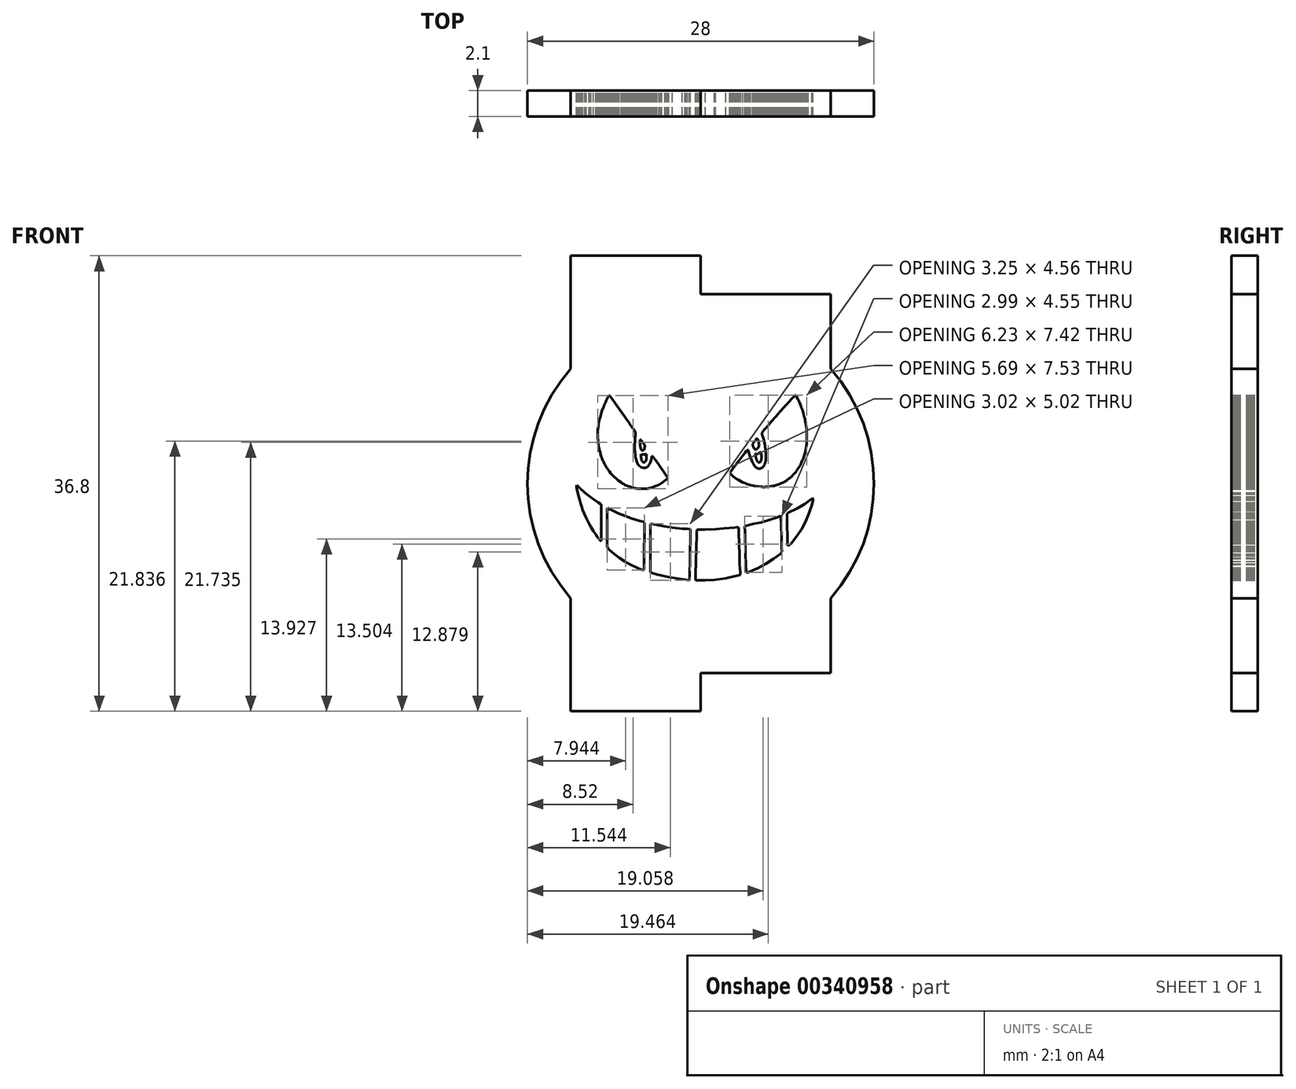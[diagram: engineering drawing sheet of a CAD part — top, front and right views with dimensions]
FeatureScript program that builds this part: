
annotation { "Feature Type Name" : "Feature", "Feature Type Description" : "" }
export const myFeature = defineFeature(function(context is Context, id is Id, definition is map)
    precondition{}
    {
        {
            var Q0;
            Q0=qCreatedBy(makeId("Front.planeOp"),FACE);
            var sketch = newSketch(context, id + "F0", { "sketchPlane" : qUnion([Q0])});
            skArc(sketch, "E0", {"start": v(-10.5, 9.26) * mm, "mid": v(-14, 0) * mm, "end": v(-10.5, -9.26) * mm});
            skLineSegment(sketch, "E1", {"start": v(-10.5, 9.26) * mm, "end": v(-10.5, 18.4) * mm});
            skLineSegment(sketch, "E2", {"start": v(-10.5, 18.4) * mm, "end": v(0, 18.4) * mm});
            skLineSegment(sketch, "E3", {"start": v(0, 18.4) * mm, "end": v(0, 15.3) * mm});
            skLineSegment(sketch, "E4", {"start": v(0, 15.3) * mm, "end": v(10.5, 15.3) * mm});
            skLineSegment(sketch, "E5", {"start": v(10.5, 15.3) * mm, "end": v(10.5, 9.26) * mm});
            skLineSegment(sketch, "E6", {"start": v(-10.5, -9.26) * mm, "end": v(-10.5, -18.4) * mm});
            skLineSegment(sketch, "E7", {"start": v(-10.5, -18.4) * mm, "end": v(0, -18.4) * mm});
            skLineSegment(sketch, "E8", {"start": v(0, -18.4) * mm, "end": v(0, -15.3) * mm});
            skLineSegment(sketch, "E9", {"start": v(0, -15.3) * mm, "end": v(10.5, -15.3) * mm});
            skLineSegment(sketch, "E10", {"start": v(10.5, -15.3) * mm, "end": v(10.5, -9.26) * mm});
            skArc(sketch, "E11.trimOffspring", {"start": v(10.5, -9.26) * mm, "mid": v(14, 0) * mm, "end": v(10.5, 9.26) * mm});
            skSolve(sketch);
        }
        {
            var Q0;
            Q0 = qSketchRegion(id + "F0", true);
            var Q1;
            Q1=makeQuery(id+"F0.imprint","IMPRINT",FACE,{"disambiguationData":[TD([[makeQuery(id+"F0.imprint","IMPRINT",EDGE,{"derivedFrom":sQuery(id+"F0.wireOp",EDGE,"E0")}),1.0]])]});
            extrude(context, id + "F1", {"entities" : qUnion([Q0, Q1]), "depth" : 2.1 * mm});
        }
        {
            var Q0;
            Q0=qCreatedBy(makeId("Front.planeOp"),FACE);
            var sketch = newSketch(context, id + "F2", { "sketchPlane" : qUnion([Q0])});
            skLineSegment(sketch, "E12", {"start": v(-7.31, 7.04) * mm, "end": v(-7.08, 6.7) * mm});
            skLineSegment(sketch, "E13", {"start": v(-7.08, 6.7) * mm, "end": v(-6.95, 6.53) * mm});
            skLineSegment(sketch, "E14", {"start": v(-6.95, 6.53) * mm, "end": v(-6.8, 6.32) * mm});
            skLineSegment(sketch, "E15", {"start": v(-6.8, 6.32) * mm, "end": v(-6.71, 6.2) * mm});
            skLineSegment(sketch, "E16", {"start": v(-6.71, 6.2) * mm, "end": v(-6.65, 6.1) * mm});
            skLineSegment(sketch, "E17", {"start": v(-6.65, 6.1) * mm, "end": v(-6.58, 6) * mm});
            skLineSegment(sketch, "E18", {"start": v(-6.58, 6) * mm, "end": v(-6.47, 5.86) * mm});
            skLineSegment(sketch, "E19", {"start": v(-6.47, 5.86) * mm, "end": v(-6.39, 5.75) * mm});
            skLineSegment(sketch, "E20", {"start": v(-6.39, 5.75) * mm, "end": v(-6.31, 5.64) * mm});
            skLineSegment(sketch, "E21", {"start": v(-6.31, 5.64) * mm, "end": v(-6.24, 5.54) * mm});
            skLineSegment(sketch, "E22", {"start": v(-6.24, 5.54) * mm, "end": v(-6.17, 5.44) * mm});
            skLineSegment(sketch, "E23", {"start": v(-6.17, 5.44) * mm, "end": v(-6.07, 5.3) * mm});
            skLineSegment(sketch, "E24", {"start": v(-6.07, 5.3) * mm, "end": v(-5.98, 5.18) * mm});
            skLineSegment(sketch, "E25", {"start": v(-5.98, 5.18) * mm, "end": v(-5.91, 5.08) * mm});
            skLineSegment(sketch, "E26", {"start": v(-5.91, 5.08) * mm, "end": v(-5.84, 4.97) * mm});
            skLineSegment(sketch, "E27", {"start": v(-5.84, 4.97) * mm, "end": v(-5.76, 4.87) * mm});
            skLineSegment(sketch, "E28", {"start": v(-5.76, 4.87) * mm, "end": v(-5.68, 4.74) * mm});
            skLineSegment(sketch, "E29", {"start": v(-5.68, 4.74) * mm, "end": v(-5.6, 4.64) * mm});
            skLineSegment(sketch, "E30", {"start": v(-5.6, 4.64) * mm, "end": v(-5.54, 4.54) * mm});
            skLineSegment(sketch, "E31", {"start": v(-5.54, 4.54) * mm, "end": v(-5.47, 4.44) * mm});
            skLineSegment(sketch, "E32", {"start": v(-5.47, 4.44) * mm, "end": v(-5.42, 4.38) * mm});
            skLineSegment(sketch, "E33", {"start": v(-5.42, 4.38) * mm, "end": v(-5.35, 4.28) * mm});
            skLineSegment(sketch, "E34", {"start": v(-5.35, 4.28) * mm, "end": v(-5.31, 4.23) * mm});
            skLineSegment(sketch, "E35", {"start": v(-5.31, 4.23) * mm, "end": v(-5.3, 4.2) * mm});
            skLineSegment(sketch, "E36", {"start": v(-5.3, 4.2) * mm, "end": v(-5.28, 4.18) * mm});
            skLineSegment(sketch, "E37", {"start": v(-5.28, 4.18) * mm, "end": v(-5.27, 4.16) * mm});
            skLineSegment(sketch, "E38", {"start": v(-5.27, 4.16) * mm, "end": v(-5.27, 4.12) * mm});
            skLineSegment(sketch, "E39", {"start": v(-5.27, 4.12) * mm, "end": v(-5.27, 4.06) * mm});
            skLineSegment(sketch, "E40", {"start": v(-5.27, 4.06) * mm, "end": v(-5.27, 4) * mm});
            skLineSegment(sketch, "E41", {"start": v(-5.27, 4) * mm, "end": v(-5.29, 3.9) * mm});
            skLineSegment(sketch, "E42", {"start": v(-5.29, 3.9) * mm, "end": v(-5.3, 3.83) * mm});
            skLineSegment(sketch, "E43", {"start": v(-5.3, 3.83) * mm, "end": v(-5.3, 3.75) * mm});
            skLineSegment(sketch, "E44", {"start": v(-5.3, 3.75) * mm, "end": v(-5.31, 3.65) * mm});
            skLineSegment(sketch, "E45", {"start": v(-5.31, 3.65) * mm, "end": v(-5.31, 3.58) * mm});
            skLineSegment(sketch, "E46", {"start": v(-5.31, 3.58) * mm, "end": v(-5.32, 3.51) * mm});
            skLineSegment(sketch, "E47", {"start": v(-5.32, 3.51) * mm, "end": v(-5.32, 3.46) * mm});
            skLineSegment(sketch, "E48", {"start": v(-5.32, 3.46) * mm, "end": v(-5.32, 3.4) * mm});
            skLineSegment(sketch, "E49", {"start": v(-5.32, 3.4) * mm, "end": v(-5.32, 3.32) * mm});
            skLineSegment(sketch, "E50", {"start": v(-5.32, 3.32) * mm, "end": v(-5.33, 3.26) * mm});
            skLineSegment(sketch, "E51", {"start": v(-5.33, 3.26) * mm, "end": v(-5.34, 3.2) * mm});
            skLineSegment(sketch, "E52", {"start": v(-5.34, 3.2) * mm, "end": v(-5.34, 3.13) * mm});
            skLineSegment(sketch, "E53", {"start": v(-5.34, 3.13) * mm, "end": v(-5.34, 3.06) * mm});
            skLineSegment(sketch, "E54", {"start": v(-5.34, 3.06) * mm, "end": v(-5.34, 3) * mm});
            skLineSegment(sketch, "E55", {"start": v(-5.34, 3) * mm, "end": v(-5.34, 2.93) * mm});
            skLineSegment(sketch, "E56", {"start": v(-5.34, 2.93) * mm, "end": v(-5.34, 2.87) * mm});
            skPoint(sketch, "E56.endSnap0", {"position": v(-5.34, 2.96) * mm});
            skLineSegment(sketch, "E57", {"start": v(-5.34, 2.87) * mm, "end": v(-5.34, 2.8) * mm});
            skLineSegment(sketch, "E58", {"start": v(-5.34, 2.8) * mm, "end": v(-5.33, 2.7) * mm});
            skLineSegment(sketch, "E59", {"start": v(-5.33, 2.7) * mm, "end": v(-5.32, 2.62) * mm});
            skLineSegment(sketch, "E60", {"start": v(-5.32, 2.62) * mm, "end": v(-5.32, 2.53) * mm});
            skLineSegment(sketch, "E61", {"start": v(-5.32, 2.53) * mm, "end": v(-5.3, 2.43) * mm});
            skLineSegment(sketch, "E62", {"start": v(-5.3, 2.43) * mm, "end": v(-5.29, 2.34) * mm});
            skLineSegment(sketch, "E63", {"start": v(-5.29, 2.34) * mm, "end": v(-5.29, 2.26) * mm});
            skLineSegment(sketch, "E64", {"start": v(-5.29, 2.26) * mm, "end": v(-5.27, 2.16) * mm});
            skLineSegment(sketch, "E65", {"start": v(-5.27, 2.16) * mm, "end": v(-5.25, 2.04) * mm});
            skLineSegment(sketch, "E66", {"start": v(-5.25, 2.04) * mm, "end": v(-5.22, 1.94) * mm});
            skLineSegment(sketch, "E67", {"start": v(-5.22, 1.94) * mm, "end": v(-5.18, 1.82) * mm});
            skLineSegment(sketch, "E68", {"start": v(-5.18, 1.82) * mm, "end": v(-5.14, 1.72) * mm});
            skLineSegment(sketch, "E69", {"start": v(-5.14, 1.72) * mm, "end": v(-5.11, 1.64) * mm});
            skLineSegment(sketch, "E70", {"start": v(-5.11, 1.64) * mm, "end": v(-5.07, 1.57) * mm});
            skLineSegment(sketch, "E71", {"start": v(-5.07, 1.57) * mm, "end": v(-5.04, 1.5) * mm});
            skLineSegment(sketch, "E72", {"start": v(-5.04, 1.5) * mm, "end": v(-5, 1.46) * mm});
            skLineSegment(sketch, "E73", {"start": v(-5, 1.46) * mm, "end": v(-4.96, 1.42) * mm});
            skLineSegment(sketch, "E74", {"start": v(-4.96, 1.42) * mm, "end": v(-4.91, 1.38) * mm});
            skLineSegment(sketch, "E75", {"start": v(-4.91, 1.38) * mm, "end": v(-4.88, 1.35) * mm});
            skLineSegment(sketch, "E76", {"start": v(-4.88, 1.35) * mm, "end": v(-4.83, 1.32) * mm});
            skLineSegment(sketch, "E77", {"start": v(-4.83, 1.32) * mm, "end": v(-4.8, 1.3) * mm});
            skLineSegment(sketch, "E78", {"start": v(-4.8, 1.3) * mm, "end": v(-4.75, 1.28) * mm});
            skLineSegment(sketch, "E79", {"start": v(-4.75, 1.28) * mm, "end": v(-4.72, 1.28) * mm});
            skLineSegment(sketch, "E80", {"start": v(-4.72, 1.28) * mm, "end": v(-4.67, 1.27) * mm});
            skLineSegment(sketch, "E81", {"start": v(-4.67, 1.27) * mm, "end": v(-4.62, 1.27) * mm});
            skLineSegment(sketch, "E82", {"start": v(-4.62, 1.27) * mm, "end": v(-4.57, 1.27) * mm});
            skLineSegment(sketch, "E83", {"start": v(-4.57, 1.27) * mm, "end": v(-4.52, 1.27) * mm});
            skLineSegment(sketch, "E84", {"start": v(-4.52, 1.27) * mm, "end": v(-4.48, 1.27) * mm});
            skLineSegment(sketch, "E85", {"start": v(-4.48, 1.27) * mm, "end": v(-4.42, 1.3) * mm});
            skLineSegment(sketch, "E86", {"start": v(-4.42, 1.3) * mm, "end": v(-4.37, 1.31) * mm});
            skLineSegment(sketch, "E87", {"start": v(-4.37, 1.31) * mm, "end": v(-4.33, 1.34) * mm});
            skLineSegment(sketch, "E88", {"start": v(-4.33, 1.34) * mm, "end": v(-4.3, 1.37) * mm});
            skLineSegment(sketch, "E89", {"start": v(-4.3, 1.37) * mm, "end": v(-4.26, 1.4) * mm});
            skLineSegment(sketch, "E90", {"start": v(-4.26, 1.4) * mm, "end": v(-4.22, 1.44) * mm});
            skLineSegment(sketch, "E91", {"start": v(-4.22, 1.44) * mm, "end": v(-4.18, 1.48) * mm});
            skLineSegment(sketch, "E92", {"start": v(-4.18, 1.48) * mm, "end": v(-4.15, 1.53) * mm});
            skLineSegment(sketch, "E93", {"start": v(-4.15, 1.53) * mm, "end": v(-4.12, 1.58) * mm});
            skLineSegment(sketch, "E94", {"start": v(-4.12, 1.58) * mm, "end": v(-4.1, 1.64) * mm});
            skLineSegment(sketch, "E95", {"start": v(-4.1, 1.64) * mm, "end": v(-4.08, 1.7) * mm});
            skLineSegment(sketch, "E96", {"start": v(-4.08, 1.7) * mm, "end": v(-4.05, 1.78) * mm});
            skLineSegment(sketch, "E97", {"start": v(-4.05, 1.78) * mm, "end": v(-4.02, 1.87) * mm});
            skLineSegment(sketch, "E98", {"start": v(-4.02, 1.87) * mm, "end": v(-4, 1.94) * mm});
            skLineSegment(sketch, "E99", {"start": v(-4, 1.94) * mm, "end": v(-3.99, 2) * mm});
            skLineSegment(sketch, "E100", {"start": v(-3.99, 2) * mm, "end": v(-3.98, 2.05) * mm});
            skLineSegment(sketch, "E101", {"start": v(-3.98, 2.05) * mm, "end": v(-3.96, 2.1) * mm});
            skLineSegment(sketch, "E102", {"start": v(-3.96, 2.1) * mm, "end": v(-3.94, 2.18) * mm});
            skLineSegment(sketch, "E103", {"start": v(-3.94, 2.18) * mm, "end": v(-3.93, 2.22) * mm});
            skLineSegment(sketch, "E104", {"start": v(-3.93, 2.22) * mm, "end": v(-3.93, 2.23) * mm});
            skLineSegment(sketch, "E105", {"start": v(-3.93, 2.23) * mm, "end": v(-3.92, 2.23) * mm});
            skLineSegment(sketch, "E106", {"start": v(-3.92, 2.23) * mm, "end": v(-3.9, 2.22) * mm});
            skLineSegment(sketch, "E107", {"start": v(-3.9, 2.22) * mm, "end": v(-3.86, 2.16) * mm});
            skLineSegment(sketch, "E108", {"start": v(-3.86, 2.16) * mm, "end": v(-3.8, 2.1) * mm});
            skLineSegment(sketch, "E109", {"start": v(-3.8, 2.1) * mm, "end": v(-3.76, 2.04) * mm});
            skLineSegment(sketch, "E110", {"start": v(-3.76, 2.04) * mm, "end": v(-3.72, 1.98) * mm});
            skLineSegment(sketch, "E111", {"start": v(-3.72, 1.98) * mm, "end": v(-3.68, 1.92) * mm});
            skLineSegment(sketch, "E112", {"start": v(-3.68, 1.92) * mm, "end": v(-3.64, 1.86) * mm});
            skLineSegment(sketch, "E113", {"start": v(-3.64, 1.86) * mm, "end": v(-3.6, 1.8) * mm});
            skLineSegment(sketch, "E114", {"start": v(-3.6, 1.8) * mm, "end": v(-3.54, 1.73) * mm});
            skLineSegment(sketch, "E115", {"start": v(-3.54, 1.73) * mm, "end": v(-3.5, 1.66) * mm});
            skLineSegment(sketch, "E116", {"start": v(-3.5, 1.66) * mm, "end": v(-3.44, 1.59) * mm});
            skLineSegment(sketch, "E117", {"start": v(-3.44, 1.59) * mm, "end": v(-3.39, 1.5) * mm});
            skLineSegment(sketch, "E118", {"start": v(-3.39, 1.5) * mm, "end": v(-3.34, 1.44) * mm});
            skLineSegment(sketch, "E119", {"start": v(-3.34, 1.44) * mm, "end": v(-3.28, 1.36) * mm});
            skLineSegment(sketch, "E120", {"start": v(-3.28, 1.36) * mm, "end": v(-3.24, 1.3) * mm});
            skLineSegment(sketch, "E121", {"start": v(-3.24, 1.3) * mm, "end": v(-3.2, 1.25) * mm});
            skLineSegment(sketch, "E122", {"start": v(-3.2, 1.25) * mm, "end": v(-3.15, 1.18) * mm});
            skLineSegment(sketch, "E123", {"start": v(-3.15, 1.18) * mm, "end": v(-3.1, 1.1) * mm});
            skLineSegment(sketch, "E124", {"start": v(-3.1, 1.1) * mm, "end": v(-3.05, 1.04) * mm});
            skLineSegment(sketch, "E125", {"start": v(-3.05, 1.04) * mm, "end": v(-3, 0.96) * mm});
            skLineSegment(sketch, "E126", {"start": v(-3, 0.96) * mm, "end": v(-2.94, 0.88) * mm});
            skLineSegment(sketch, "E127", {"start": v(-2.94, 0.88) * mm, "end": v(-2.89, 0.81) * mm});
            skLineSegment(sketch, "E128", {"start": v(-2.89, 0.81) * mm, "end": v(-2.84, 0.74) * mm});
            skLineSegment(sketch, "E129", {"start": v(-2.84, 0.74) * mm, "end": v(-2.8, 0.7) * mm});
            skLineSegment(sketch, "E130", {"start": v(-2.8, 0.7) * mm, "end": v(-2.76, 0.63) * mm});
            skLineSegment(sketch, "E131", {"start": v(-2.76, 0.63) * mm, "end": v(-2.72, 0.57) * mm});
            skLineSegment(sketch, "E132", {"start": v(-2.72, 0.57) * mm, "end": v(-2.69, 0.53) * mm});
            skLineSegment(sketch, "E133", {"start": v(-2.69, 0.53) * mm, "end": v(-2.66, 0.5) * mm});
            skLineSegment(sketch, "E134", {"start": v(-2.66, 0.5) * mm, "end": v(-2.65, 0.47) * mm});
            skLineSegment(sketch, "E135", {"start": v(-2.65, 0.47) * mm, "end": v(-2.64, 0.46) * mm});
            skLineSegment(sketch, "E136", {"start": v(-2.64, 0.46) * mm, "end": v(-2.63, 0.46) * mm});
            skLineSegment(sketch, "E137", {"start": v(-2.63, 0.46) * mm, "end": v(-2.64, 0.45) * mm});
            skLineSegment(sketch, "E138", {"start": v(-2.64, 0.45) * mm, "end": v(-2.66, 0.43) * mm});
            skLineSegment(sketch, "E139", {"start": v(-2.66, 0.43) * mm, "end": v(-2.7, 0.39) * mm});
            skLineSegment(sketch, "E140", {"start": v(-2.7, 0.39) * mm, "end": v(-2.75, 0.34) * mm});
            skLineSegment(sketch, "E141", {"start": v(-2.75, 0.34) * mm, "end": v(-2.8, 0.3) * mm});
            skLineSegment(sketch, "E142", {"start": v(-2.8, 0.3) * mm, "end": v(-2.83, 0.28) * mm});
            skLineSegment(sketch, "E143", {"start": v(-2.83, 0.28) * mm, "end": v(-2.89, 0.24) * mm});
            skLineSegment(sketch, "E144", {"start": v(-2.89, 0.24) * mm, "end": v(-2.94, 0.2) * mm});
            skLineSegment(sketch, "E145", {"start": v(-2.94, 0.2) * mm, "end": v(-3, 0.16) * mm});
            skLineSegment(sketch, "E146", {"start": v(-3, 0.16) * mm, "end": v(-3.04, 0.13) * mm});
            skLineSegment(sketch, "E147", {"start": v(-3.04, 0.13) * mm, "end": v(-3.1, 0.1) * mm});
            skLineSegment(sketch, "E148", {"start": v(-3.1, 0.1) * mm, "end": v(-3.15, 0.05) * mm});
            skLineSegment(sketch, "E149", {"start": v(-3.15, 0.05) * mm, "end": v(-3.21, 0) * mm});
            skLineSegment(sketch, "E150", {"start": v(-3.21, 0) * mm, "end": v(-3.26, -0.02) * mm});
            skLineSegment(sketch, "E151", {"start": v(-3.26, -0.02) * mm, "end": v(-3.32, -0.05) * mm});
            skLineSegment(sketch, "E152", {"start": v(-3.32, -0.05) * mm, "end": v(-3.39, -0.1) * mm});
            skLineSegment(sketch, "E153", {"start": v(-3.39, -0.1) * mm, "end": v(-3.46, -0.13) * mm});
            skLineSegment(sketch, "E154", {"start": v(-3.46, -0.13) * mm, "end": v(-3.53, -0.16) * mm});
            skLineSegment(sketch, "E155", {"start": v(-3.53, -0.16) * mm, "end": v(-3.57, -0.19) * mm});
            skLineSegment(sketch, "E156", {"start": v(-3.57, -0.19) * mm, "end": v(-3.64, -0.2) * mm});
            skLineSegment(sketch, "E157", {"start": v(-3.64, -0.2) * mm, "end": v(-3.73, -0.24) * mm});
            skLineSegment(sketch, "E158", {"start": v(-3.73, -0.24) * mm, "end": v(-3.8, -0.26) * mm});
            skLineSegment(sketch, "E159", {"start": v(-3.8, -0.26) * mm, "end": v(-3.86, -0.28) * mm});
            skLineSegment(sketch, "E160", {"start": v(-3.86, -0.28) * mm, "end": v(-3.93, -0.3) * mm});
            skLineSegment(sketch, "E161", {"start": v(-3.93, -0.3) * mm, "end": v(-3.99, -0.33) * mm});
            skLineSegment(sketch, "E162", {"start": v(-3.99, -0.33) * mm, "end": v(-4.03, -0.34) * mm});
            skLineSegment(sketch, "E163", {"start": v(-4.03, -0.34) * mm, "end": v(-4.1, -0.36) * mm});
            skLineSegment(sketch, "E164", {"start": v(-4.1, -0.36) * mm, "end": v(-4.14, -0.37) * mm});
            skLineSegment(sketch, "E165", {"start": v(-4.14, -0.37) * mm, "end": v(-4.22, -0.38) * mm});
            skLineSegment(sketch, "E166", {"start": v(-4.22, -0.38) * mm, "end": v(-4.3, -0.4) * mm});
            skLineSegment(sketch, "E167", {"start": v(-4.3, -0.4) * mm, "end": v(-4.37, -0.4) * mm});
            skLineSegment(sketch, "E168", {"start": v(-4.37, -0.4) * mm, "end": v(-4.43, -0.42) * mm});
            skLineSegment(sketch, "E169", {"start": v(-4.43, -0.42) * mm, "end": v(-4.52, -0.43) * mm});
            skLineSegment(sketch, "E170", {"start": v(-4.52, -0.43) * mm, "end": v(-4.59, -0.43) * mm});
            skLineSegment(sketch, "E171", {"start": v(-4.59, -0.43) * mm, "end": v(-4.67, -0.43) * mm});
            skLineSegment(sketch, "E172", {"start": v(-4.67, -0.43) * mm, "end": v(-4.78, -0.43) * mm});
            skLineSegment(sketch, "E173", {"start": v(-4.78, -0.43) * mm, "end": v(-4.88, -0.43) * mm});
            skLineSegment(sketch, "E174", {"start": v(-4.88, -0.43) * mm, "end": v(-5, -0.42) * mm});
            skLineSegment(sketch, "E175", {"start": v(-5, -0.42) * mm, "end": v(-5.13, -0.4) * mm});
            skLineSegment(sketch, "E176", {"start": v(-5.13, -0.4) * mm, "end": v(-5.24, -0.39) * mm});
            skLineSegment(sketch, "E177", {"start": v(-5.24, -0.39) * mm, "end": v(-5.32, -0.37) * mm});
            skLineSegment(sketch, "E178", {"start": v(-5.32, -0.37) * mm, "end": v(-5.4, -0.36) * mm});
            skLineSegment(sketch, "E179", {"start": v(-5.4, -0.36) * mm, "end": v(-5.49, -0.34) * mm});
            skLineSegment(sketch, "E180", {"start": v(-5.49, -0.34) * mm, "end": v(-5.57, -0.31) * mm});
            skLineSegment(sketch, "E181", {"start": v(-5.57, -0.31) * mm, "end": v(-5.7, -0.27) * mm});
            skLineSegment(sketch, "E182", {"start": v(-5.7, -0.27) * mm, "end": v(-5.83, -0.22) * mm});
            skLineSegment(sketch, "E183", {"start": v(-5.83, -0.22) * mm, "end": v(-5.97, -0.17) * mm});
            skLineSegment(sketch, "E184", {"start": v(-5.97, -0.17) * mm, "end": v(-6.09, -0.12) * mm});
            skLineSegment(sketch, "E185", {"start": v(-6.09, -0.12) * mm, "end": v(-6.16, -0.08) * mm});
            skLineSegment(sketch, "E186", {"start": v(-6.16, -0.08) * mm, "end": v(-6.24, -0.04) * mm});
            skLineSegment(sketch, "E187", {"start": v(-6.24, -0.04) * mm, "end": v(-6.3, 0) * mm});
            skLineSegment(sketch, "E188", {"start": v(-6.3, 0) * mm, "end": v(-6.36, 0.03) * mm});
            skLineSegment(sketch, "E189", {"start": v(-6.36, 0.03) * mm, "end": v(-6.43, 0.08) * mm});
            skLineSegment(sketch, "E190", {"start": v(-6.43, 0.08) * mm, "end": v(-6.5, 0.14) * mm});
            skLineSegment(sketch, "E191", {"start": v(-6.5, 0.14) * mm, "end": v(-6.58, 0.2) * mm});
            skLineSegment(sketch, "E192", {"start": v(-6.58, 0.2) * mm, "end": v(-6.67, 0.26) * mm});
            skLineSegment(sketch, "E193", {"start": v(-6.67, 0.26) * mm, "end": v(-6.77, 0.33) * mm});
            skLineSegment(sketch, "E194", {"start": v(-6.77, 0.33) * mm, "end": v(-6.85, 0.4) * mm});
            skLineSegment(sketch, "E195", {"start": v(-6.85, 0.4) * mm, "end": v(-6.9, 0.46) * mm});
            skLineSegment(sketch, "E196", {"start": v(-6.9, 0.46) * mm, "end": v(-6.96, 0.5) * mm});
            skLineSegment(sketch, "E197", {"start": v(-6.96, 0.5) * mm, "end": v(-7.02, 0.57) * mm});
            skLineSegment(sketch, "E198", {"start": v(-7.02, 0.57) * mm, "end": v(-7.1, 0.64) * mm});
            skLineSegment(sketch, "E199", {"start": v(-7.1, 0.64) * mm, "end": v(-7.15, 0.7) * mm});
            skLineSegment(sketch, "E200", {"start": v(-7.15, 0.7) * mm, "end": v(-7.2, 0.76) * mm});
            skLineSegment(sketch, "E201", {"start": v(-7.2, 0.76) * mm, "end": v(-7.27, 0.83) * mm});
            skLineSegment(sketch, "E202", {"start": v(-7.27, 0.83) * mm, "end": v(-7.32, 0.9) * mm});
            skLineSegment(sketch, "E203", {"start": v(-7.32, 0.9) * mm, "end": v(-7.37, 0.98) * mm});
            skLineSegment(sketch, "E204", {"start": v(-7.37, 0.98) * mm, "end": v(-7.44, 1.06) * mm});
            skLineSegment(sketch, "E205", {"start": v(-7.44, 1.06) * mm, "end": v(-7.5, 1.13) * mm});
            skLineSegment(sketch, "E206", {"start": v(-7.5, 1.13) * mm, "end": v(-7.54, 1.2) * mm});
            skLineSegment(sketch, "E207", {"start": v(-7.54, 1.2) * mm, "end": v(-7.6, 1.27) * mm});
            skLineSegment(sketch, "E208", {"start": v(-7.6, 1.27) * mm, "end": v(-7.65, 1.35) * mm});
            skLineSegment(sketch, "E209", {"start": v(-7.65, 1.35) * mm, "end": v(-7.7, 1.43) * mm});
            skLineSegment(sketch, "E210", {"start": v(-7.7, 1.43) * mm, "end": v(-7.73, 1.5) * mm});
            skLineSegment(sketch, "E211", {"start": v(-7.73, 1.5) * mm, "end": v(-7.78, 1.6) * mm});
            skLineSegment(sketch, "E212", {"start": v(-7.78, 1.6) * mm, "end": v(-7.82, 1.68) * mm});
            skLineSegment(sketch, "E213", {"start": v(-7.82, 1.68) * mm, "end": v(-7.86, 1.76) * mm});
            skLineSegment(sketch, "E214", {"start": v(-7.86, 1.76) * mm, "end": v(-7.9, 1.85) * mm});
            skLineSegment(sketch, "E215", {"start": v(-7.9, 1.85) * mm, "end": v(-7.95, 1.94) * mm});
            skLineSegment(sketch, "E216", {"start": v(-7.95, 1.94) * mm, "end": v(-7.98, 2.04) * mm});
            skLineSegment(sketch, "E217", {"start": v(-7.98, 2.04) * mm, "end": v(-8.01, 2.09) * mm});
            skLineSegment(sketch, "E218", {"start": v(-8.01, 2.09) * mm, "end": v(-8.05, 2.2) * mm});
            skLineSegment(sketch, "E219", {"start": v(-8.05, 2.2) * mm, "end": v(-8.08, 2.3) * mm});
            skLineSegment(sketch, "E220", {"start": v(-8.08, 2.3) * mm, "end": v(-8.1, 2.38) * mm});
            skLineSegment(sketch, "E221", {"start": v(-8.1, 2.38) * mm, "end": v(-8.12, 2.46) * mm});
            skLineSegment(sketch, "E222", {"start": v(-8.12, 2.46) * mm, "end": v(-8.14, 2.56) * mm});
            skLineSegment(sketch, "E223", {"start": v(-8.14, 2.56) * mm, "end": v(-8.17, 2.65) * mm});
            skLineSegment(sketch, "E224", {"start": v(-8.17, 2.65) * mm, "end": v(-8.2, 2.75) * mm});
            skLineSegment(sketch, "E225", {"start": v(-8.2, 2.75) * mm, "end": v(-8.21, 2.83) * mm});
            skLineSegment(sketch, "E226", {"start": v(-8.21, 2.83) * mm, "end": v(-8.23, 2.92) * mm});
            skLineSegment(sketch, "E227", {"start": v(-8.23, 2.92) * mm, "end": v(-8.25, 3.04) * mm});
            skLineSegment(sketch, "E228", {"start": v(-8.25, 3.04) * mm, "end": v(-8.26, 3.13) * mm});
            skLineSegment(sketch, "E229", {"start": v(-8.26, 3.13) * mm, "end": v(-8.28, 3.23) * mm});
            skLineSegment(sketch, "E230", {"start": v(-8.28, 3.23) * mm, "end": v(-8.29, 3.33) * mm});
            skLineSegment(sketch, "E231", {"start": v(-8.29, 3.33) * mm, "end": v(-8.3, 3.42) * mm});
            skLineSegment(sketch, "E232", {"start": v(-8.3, 3.42) * mm, "end": v(-8.3, 3.52) * mm});
            skLineSegment(sketch, "E233", {"start": v(-8.3, 3.52) * mm, "end": v(-8.32, 3.65) * mm});
            skLineSegment(sketch, "E234", {"start": v(-8.32, 3.65) * mm, "end": v(-8.32, 3.77) * mm});
            skLineSegment(sketch, "E235", {"start": v(-8.32, 3.77) * mm, "end": v(-8.32, 3.86) * mm});
            skLineSegment(sketch, "E236", {"start": v(-8.32, 3.86) * mm, "end": v(-8.33, 3.99) * mm});
            skLineSegment(sketch, "E237", {"start": v(-8.33, 3.99) * mm, "end": v(-8.33, 4.12) * mm});
            skLineSegment(sketch, "E238", {"start": v(-8.33, 4.12) * mm, "end": v(-8.33, 4.2) * mm});
            skLineSegment(sketch, "E239", {"start": v(-8.33, 4.2) * mm, "end": v(-8.31, 4.33) * mm});
            skLineSegment(sketch, "E240", {"start": v(-8.31, 4.33) * mm, "end": v(-8.3, 4.44) * mm});
            skLineSegment(sketch, "E241", {"start": v(-8.3, 4.44) * mm, "end": v(-8.29, 4.53) * mm});
            skLineSegment(sketch, "E242", {"start": v(-8.29, 4.53) * mm, "end": v(-8.27, 4.63) * mm});
            skLineSegment(sketch, "E243", {"start": v(-8.27, 4.63) * mm, "end": v(-8.25, 4.77) * mm});
            skLineSegment(sketch, "E244", {"start": v(-8.25, 4.77) * mm, "end": v(-8.22, 4.97) * mm});
            skLineSegment(sketch, "E245", {"start": v(-8.22, 4.97) * mm, "end": v(-8.19, 5.15) * mm});
            skLineSegment(sketch, "E246", {"start": v(-8.19, 5.15) * mm, "end": v(-8.15, 5.28) * mm});
            skLineSegment(sketch, "E247", {"start": v(-8.15, 5.28) * mm, "end": v(-8.1, 5.4) * mm});
            skLineSegment(sketch, "E248", {"start": v(-8.1, 5.4) * mm, "end": v(-8.08, 5.54) * mm});
            skLineSegment(sketch, "E249", {"start": v(-8.08, 5.54) * mm, "end": v(-8.04, 5.7) * mm});
            skLineSegment(sketch, "E250", {"start": v(-8.04, 5.7) * mm, "end": v(-8, 5.8) * mm});
            skLineSegment(sketch, "E251", {"start": v(-8, 5.8) * mm, "end": v(-7.97, 5.9) * mm});
            skLineSegment(sketch, "E252", {"start": v(-7.97, 5.9) * mm, "end": v(-7.93, 6.02) * mm});
            skLineSegment(sketch, "E253", {"start": v(-7.93, 6.02) * mm, "end": v(-7.88, 6.14) * mm});
            skLineSegment(sketch, "E254", {"start": v(-7.88, 6.14) * mm, "end": v(-7.83, 6.25) * mm});
            skLineSegment(sketch, "E255", {"start": v(-7.83, 6.25) * mm, "end": v(-7.8, 6.33) * mm});
            skLineSegment(sketch, "E256", {"start": v(-7.8, 6.33) * mm, "end": v(-7.77, 6.4) * mm});
            skLineSegment(sketch, "E257", {"start": v(-7.77, 6.4) * mm, "end": v(-7.74, 6.45) * mm});
            skLineSegment(sketch, "E258", {"start": v(-7.74, 6.45) * mm, "end": v(-7.7, 6.54) * mm});
            skLineSegment(sketch, "E259", {"start": v(-7.7, 6.54) * mm, "end": v(-7.65, 6.65) * mm});
            skLineSegment(sketch, "E260", {"start": v(-7.65, 6.65) * mm, "end": v(-7.6, 6.78) * mm});
            skLineSegment(sketch, "E261", {"start": v(-7.6, 6.78) * mm, "end": v(-7.57, 6.85) * mm});
            skLineSegment(sketch, "E262", {"start": v(-7.57, 6.85) * mm, "end": v(-7.52, 6.92) * mm});
            skLineSegment(sketch, "E263", {"start": v(-7.52, 6.92) * mm, "end": v(-7.5, 6.97) * mm});
            skLineSegment(sketch, "E264", {"start": v(-7.5, 6.97) * mm, "end": v(-7.45, 7.04) * mm});
            skLineSegment(sketch, "E265", {"start": v(-7.45, 7.04) * mm, "end": v(-7.42, 7.07) * mm});
            skLineSegment(sketch, "E266", {"start": v(-7.42, 7.07) * mm, "end": v(-7.4, 7.1) * mm});
            skLineSegment(sketch, "E267", {"start": v(-7.4, 7.1) * mm, "end": v(-7.4, 7.1) * mm});
            skLineSegment(sketch, "E268", {"start": v(-7.4, 7.1) * mm, "end": v(-7.38, 7.1) * mm});
            skLineSegment(sketch, "E269", {"start": v(-7.38, 7.1) * mm, "end": v(-7.37, 7.1) * mm});
            skLineSegment(sketch, "E270", {"start": v(-7.37, 7.1) * mm, "end": v(-7.35, 7.08) * mm});
            skLineSegment(sketch, "E271", {"start": v(-7.35, 7.08) * mm, "end": v(-7.34, 7.07) * mm});
            skLineSegment(sketch, "E272", {"start": v(-7.34, 7.07) * mm, "end": v(-7.32, 7.06) * mm});
            skLineSegment(sketch, "E273", {"start": v(-7.32, 7.06) * mm, "end": v(-7.31, 7.04) * mm});
            skLineSegment(sketch, "E274", {"start": v(-4.84, 2.37) * mm, "end": v(-4.8, 2.36) * mm});
            skLineSegment(sketch, "E275", {"start": v(-4.8, 2.36) * mm, "end": v(-4.78, 2.35) * mm});
            skLineSegment(sketch, "E276", {"start": v(-4.78, 2.35) * mm, "end": v(-4.76, 2.35) * mm});
            skLineSegment(sketch, "E277", {"start": v(-4.76, 2.35) * mm, "end": v(-4.73, 2.34) * mm});
            skLineSegment(sketch, "E278", {"start": v(-4.73, 2.34) * mm, "end": v(-4.7, 2.34) * mm});
            skLineSegment(sketch, "E279", {"start": v(-4.7, 2.34) * mm, "end": v(-4.67, 2.34) * mm});
            skLineSegment(sketch, "E280", {"start": v(-4.67, 2.34) * mm, "end": v(-4.63, 2.34) * mm});
            skLineSegment(sketch, "E281", {"start": v(-4.63, 2.34) * mm, "end": v(-4.6, 2.34) * mm});
            skLineSegment(sketch, "E282", {"start": v(-4.6, 2.34) * mm, "end": v(-4.58, 2.33) * mm});
            skLineSegment(sketch, "E283", {"start": v(-4.58, 2.33) * mm, "end": v(-4.54, 2.34) * mm});
            skLineSegment(sketch, "E284", {"start": v(-4.54, 2.34) * mm, "end": v(-4.52, 2.34) * mm});
            skLineSegment(sketch, "E285", {"start": v(-4.52, 2.34) * mm, "end": v(-4.49, 2.35) * mm});
            skLineSegment(sketch, "E286", {"start": v(-4.49, 2.35) * mm, "end": v(-4.47, 2.36) * mm});
            skLineSegment(sketch, "E287", {"start": v(-4.47, 2.36) * mm, "end": v(-4.44, 2.37) * mm});
            skLineSegment(sketch, "E288", {"start": v(-4.44, 2.37) * mm, "end": v(-4.42, 2.38) * mm});
            skLineSegment(sketch, "E289", {"start": v(-4.42, 2.38) * mm, "end": v(-4.4, 2.38) * mm});
            skLineSegment(sketch, "E290", {"start": v(-4.4, 2.38) * mm, "end": v(-4.4, 2.38) * mm});
            skLineSegment(sketch, "E291", {"start": v(-4.4, 2.38) * mm, "end": v(-4.4, 2.35) * mm});
            skLineSegment(sketch, "E292", {"start": v(-4.4, 2.35) * mm, "end": v(-4.4, 2.31) * mm});
            skLineSegment(sketch, "E293", {"start": v(-4.4, 2.31) * mm, "end": v(-4.4, 2.26) * mm});
            skLineSegment(sketch, "E294", {"start": v(-4.4, 2.26) * mm, "end": v(-4.4, 2.2) * mm});
            skLineSegment(sketch, "E295", {"start": v(-4.4, 2.2) * mm, "end": v(-4.4, 2.13) * mm});
            skLineSegment(sketch, "E296", {"start": v(-4.4, 2.13) * mm, "end": v(-4.4, 2.07) * mm});
            skLineSegment(sketch, "E297", {"start": v(-4.4, 2.07) * mm, "end": v(-4.4, 2.02) * mm});
            skLineSegment(sketch, "E298", {"start": v(-4.4, 2.02) * mm, "end": v(-4.4, 1.98) * mm});
            skLineSegment(sketch, "E299", {"start": v(-4.4, 1.98) * mm, "end": v(-4.4, 1.95) * mm});
            skLineSegment(sketch, "E300", {"start": v(-4.4, 1.95) * mm, "end": v(-4.42, 1.92) * mm});
            skLineSegment(sketch, "E301", {"start": v(-4.42, 1.92) * mm, "end": v(-4.43, 1.88) * mm});
            skLineSegment(sketch, "E302", {"start": v(-4.43, 1.88) * mm, "end": v(-4.44, 1.84) * mm});
            skLineSegment(sketch, "E303", {"start": v(-4.44, 1.84) * mm, "end": v(-4.46, 1.8) * mm});
            skLineSegment(sketch, "E304", {"start": v(-4.46, 1.8) * mm, "end": v(-4.48, 1.77) * mm});
            skLineSegment(sketch, "E305", {"start": v(-4.48, 1.77) * mm, "end": v(-4.5, 1.75) * mm});
            skLineSegment(sketch, "E306", {"start": v(-4.5, 1.75) * mm, "end": v(-4.53, 1.73) * mm});
            skLineSegment(sketch, "E307", {"start": v(-4.53, 1.73) * mm, "end": v(-4.54, 1.72) * mm});
            skLineSegment(sketch, "E308", {"start": v(-4.54, 1.72) * mm, "end": v(-4.56, 1.7) * mm});
            skLineSegment(sketch, "E309", {"start": v(-4.56, 1.7) * mm, "end": v(-4.58, 1.7) * mm});
            skLineSegment(sketch, "E310", {"start": v(-4.58, 1.7) * mm, "end": v(-4.6, 1.7) * mm});
            skLineSegment(sketch, "E311", {"start": v(-4.6, 1.7) * mm, "end": v(-4.62, 1.7) * mm});
            skLineSegment(sketch, "E312", {"start": v(-4.62, 1.7) * mm, "end": v(-4.64, 1.7) * mm});
            skLineSegment(sketch, "E313", {"start": v(-4.64, 1.7) * mm, "end": v(-4.65, 1.71) * mm});
            skLineSegment(sketch, "E314", {"start": v(-4.65, 1.71) * mm, "end": v(-4.67, 1.73) * mm});
            skLineSegment(sketch, "E315", {"start": v(-4.67, 1.73) * mm, "end": v(-4.7, 1.75) * mm});
            skLineSegment(sketch, "E316", {"start": v(-4.7, 1.75) * mm, "end": v(-4.72, 1.77) * mm});
            skLineSegment(sketch, "E317", {"start": v(-4.72, 1.77) * mm, "end": v(-4.74, 1.8) * mm});
            skLineSegment(sketch, "E318", {"start": v(-4.74, 1.8) * mm, "end": v(-4.75, 1.83) * mm});
            skLineSegment(sketch, "E319", {"start": v(-4.75, 1.83) * mm, "end": v(-4.76, 1.85) * mm});
            skLineSegment(sketch, "E320", {"start": v(-4.76, 1.85) * mm, "end": v(-4.77, 1.87) * mm});
            skLineSegment(sketch, "E321", {"start": v(-4.77, 1.87) * mm, "end": v(-4.78, 1.9) * mm});
            skLineSegment(sketch, "E322", {"start": v(-4.78, 1.9) * mm, "end": v(-4.79, 1.94) * mm});
            skLineSegment(sketch, "E323", {"start": v(-4.79, 1.94) * mm, "end": v(-4.8, 1.98) * mm});
            skLineSegment(sketch, "E324", {"start": v(-4.8, 1.98) * mm, "end": v(-4.8, 2.05) * mm});
            skLineSegment(sketch, "E325", {"start": v(-4.8, 2.05) * mm, "end": v(-4.8, 2.08) * mm});
            skLineSegment(sketch, "E326", {"start": v(-4.8, 2.08) * mm, "end": v(-4.82, 2.12) * mm});
            skLineSegment(sketch, "E327", {"start": v(-4.82, 2.12) * mm, "end": v(-4.82, 2.15) * mm});
            skLineSegment(sketch, "E328", {"start": v(-4.82, 2.15) * mm, "end": v(-4.82, 2.18) * mm});
            skLineSegment(sketch, "E329", {"start": v(-4.82, 2.18) * mm, "end": v(-4.82, 2.21) * mm});
            skLineSegment(sketch, "E330", {"start": v(-4.82, 2.21) * mm, "end": v(-4.83, 2.24) * mm});
            skLineSegment(sketch, "E331", {"start": v(-4.83, 2.24) * mm, "end": v(-4.83, 2.26) * mm});
            skLineSegment(sketch, "E332", {"start": v(-4.83, 2.26) * mm, "end": v(-4.83, 2.29) * mm});
            skLineSegment(sketch, "E333", {"start": v(-4.83, 2.29) * mm, "end": v(-4.84, 2.31) * mm});
            skLineSegment(sketch, "E334", {"start": v(-4.84, 2.31) * mm, "end": v(-4.84, 2.33) * mm});
            skLineSegment(sketch, "E335", {"start": v(-4.84, 2.33) * mm, "end": v(-4.84, 2.35) * mm});
            skLineSegment(sketch, "E336", {"start": v(-4.84, 2.35) * mm, "end": v(-4.84, 2.37) * mm});
            skLineSegment(sketch, "E337", {"start": v(-4.84, 2.37) * mm, "end": v(-4.84, 2.37) * mm});
            skLineSegment(sketch, "E338", {"start": v(4.42, 2.4) * mm, "end": v(4.45, 2.4) * mm});
            skLineSegment(sketch, "E339", {"start": v(4.45, 2.4) * mm, "end": v(4.48, 2.39) * mm});
            skLineSegment(sketch, "E340", {"start": v(4.48, 2.39) * mm, "end": v(4.5, 2.39) * mm});
            skLineSegment(sketch, "E341", {"start": v(4.5, 2.39) * mm, "end": v(4.54, 2.38) * mm});
            skLineSegment(sketch, "E342", {"start": v(4.54, 2.38) * mm, "end": v(4.57, 2.39) * mm});
            skLineSegment(sketch, "E343", {"start": v(4.57, 2.39) * mm, "end": v(4.6, 2.39) * mm});
            skLineSegment(sketch, "E344", {"start": v(4.6, 2.39) * mm, "end": v(4.63, 2.4) * mm});
            skLineSegment(sketch, "E345", {"start": v(4.63, 2.4) * mm, "end": v(4.66, 2.41) * mm});
            skLineSegment(sketch, "E346", {"start": v(4.66, 2.41) * mm, "end": v(4.69, 2.43) * mm});
            skLineSegment(sketch, "E347", {"start": v(4.69, 2.43) * mm, "end": v(4.7, 2.45) * mm});
            skLineSegment(sketch, "E348", {"start": v(4.7, 2.45) * mm, "end": v(4.74, 2.48) * mm});
            skLineSegment(sketch, "E349", {"start": v(4.74, 2.48) * mm, "end": v(4.76, 2.5) * mm});
            skLineSegment(sketch, "E350", {"start": v(4.76, 2.5) * mm, "end": v(4.8, 2.52) * mm});
            skLineSegment(sketch, "E351", {"start": v(4.8, 2.52) * mm, "end": v(4.8, 2.54) * mm});
            skLineSegment(sketch, "E352", {"start": v(4.8, 2.54) * mm, "end": v(4.82, 2.55) * mm});
            skLineSegment(sketch, "E353", {"start": v(4.82, 2.55) * mm, "end": v(4.84, 2.54) * mm});
            skLineSegment(sketch, "E354", {"start": v(4.84, 2.54) * mm, "end": v(4.85, 2.52) * mm});
            skLineSegment(sketch, "E355", {"start": v(4.85, 2.52) * mm, "end": v(4.86, 2.48) * mm});
            skLineSegment(sketch, "E356", {"start": v(4.86, 2.48) * mm, "end": v(4.88, 2.43) * mm});
            skLineSegment(sketch, "E357", {"start": v(4.88, 2.43) * mm, "end": v(4.89, 2.38) * mm});
            skLineSegment(sketch, "E358", {"start": v(4.89, 2.38) * mm, "end": v(4.9, 2.33) * mm});
            skLineSegment(sketch, "E359", {"start": v(4.9, 2.33) * mm, "end": v(4.9, 2.3) * mm});
            skLineSegment(sketch, "E360", {"start": v(4.9, 2.3) * mm, "end": v(4.9, 2.25) * mm});
            skLineSegment(sketch, "E361", {"start": v(4.9, 2.25) * mm, "end": v(4.91, 2.21) * mm});
            skLineSegment(sketch, "E362", {"start": v(4.91, 2.21) * mm, "end": v(4.91, 2.18) * mm});
            skLineSegment(sketch, "E363", {"start": v(4.91, 2.18) * mm, "end": v(4.91, 2.15) * mm});
            skLineSegment(sketch, "E364", {"start": v(4.91, 2.15) * mm, "end": v(4.91, 2.11) * mm});
            skLineSegment(sketch, "E365", {"start": v(4.91, 2.11) * mm, "end": v(4.91, 2.08) * mm});
            skLineSegment(sketch, "E366", {"start": v(4.91, 2.08) * mm, "end": v(4.91, 2.05) * mm});
            skLineSegment(sketch, "E367", {"start": v(4.91, 2.05) * mm, "end": v(4.9, 2.02) * mm});
            skLineSegment(sketch, "E368", {"start": v(4.9, 2.02) * mm, "end": v(4.9, 1.99) * mm});
            skLineSegment(sketch, "E369", {"start": v(4.9, 1.99) * mm, "end": v(4.9, 1.95) * mm});
            skLineSegment(sketch, "E370", {"start": v(4.9, 1.95) * mm, "end": v(4.9, 1.92) * mm});
            skLineSegment(sketch, "E371", {"start": v(4.9, 1.92) * mm, "end": v(4.88, 1.88) * mm});
            skLineSegment(sketch, "E372", {"start": v(4.88, 1.88) * mm, "end": v(4.87, 1.85) * mm});
            skLineSegment(sketch, "E373", {"start": v(4.87, 1.85) * mm, "end": v(4.85, 1.82) * mm});
            skLineSegment(sketch, "E374", {"start": v(4.85, 1.82) * mm, "end": v(4.84, 1.8) * mm});
            skLineSegment(sketch, "E375", {"start": v(4.84, 1.8) * mm, "end": v(4.83, 1.77) * mm});
            skLineSegment(sketch, "E376", {"start": v(4.83, 1.77) * mm, "end": v(4.8, 1.74) * mm});
            skLineSegment(sketch, "E377", {"start": v(4.8, 1.74) * mm, "end": v(4.79, 1.72) * mm});
            skLineSegment(sketch, "E378", {"start": v(4.79, 1.72) * mm, "end": v(4.76, 1.7) * mm});
            skLineSegment(sketch, "E379", {"start": v(4.76, 1.7) * mm, "end": v(4.75, 1.7) * mm});
            skLineSegment(sketch, "E380", {"start": v(4.75, 1.7) * mm, "end": v(4.72, 1.7) * mm});
            skLineSegment(sketch, "E381", {"start": v(4.72, 1.7) * mm, "end": v(4.7, 1.7) * mm});
            skLineSegment(sketch, "E382", {"start": v(4.7, 1.7) * mm, "end": v(4.68, 1.7) * mm});
            skLineSegment(sketch, "E383", {"start": v(4.68, 1.7) * mm, "end": v(4.66, 1.71) * mm});
            skLineSegment(sketch, "E384", {"start": v(4.66, 1.71) * mm, "end": v(4.63, 1.73) * mm});
            skLineSegment(sketch, "E385", {"start": v(4.63, 1.73) * mm, "end": v(4.6, 1.76) * mm});
            skLineSegment(sketch, "E386", {"start": v(4.6, 1.76) * mm, "end": v(4.6, 1.78) * mm});
            skLineSegment(sketch, "E387", {"start": v(4.6, 1.78) * mm, "end": v(4.58, 1.8) * mm});
            skLineSegment(sketch, "E388", {"start": v(4.58, 1.8) * mm, "end": v(4.56, 1.83) * mm});
            skLineSegment(sketch, "E389", {"start": v(4.56, 1.83) * mm, "end": v(4.55, 1.86) * mm});
            skLineSegment(sketch, "E390", {"start": v(4.55, 1.86) * mm, "end": v(4.54, 1.88) * mm});
            skLineSegment(sketch, "E391", {"start": v(4.54, 1.88) * mm, "end": v(4.53, 1.9) * mm});
            skLineSegment(sketch, "E392", {"start": v(4.53, 1.9) * mm, "end": v(4.51, 1.94) * mm});
            skLineSegment(sketch, "E393", {"start": v(4.51, 1.94) * mm, "end": v(4.5, 1.98) * mm});
            skLineSegment(sketch, "E394", {"start": v(4.5, 1.98) * mm, "end": v(4.48, 2.03) * mm});
            skLineSegment(sketch, "E395", {"start": v(4.48, 2.03) * mm, "end": v(4.47, 2.08) * mm});
            skLineSegment(sketch, "E396", {"start": v(4.47, 2.08) * mm, "end": v(4.46, 2.11) * mm});
            skLineSegment(sketch, "E397", {"start": v(4.46, 2.11) * mm, "end": v(4.45, 2.15) * mm});
            skLineSegment(sketch, "E398", {"start": v(4.45, 2.15) * mm, "end": v(4.45, 2.18) * mm});
            skLineSegment(sketch, "E399", {"start": v(4.45, 2.18) * mm, "end": v(4.45, 2.22) * mm});
            skLineSegment(sketch, "E400", {"start": v(4.45, 2.22) * mm, "end": v(4.44, 2.27) * mm});
            skLineSegment(sketch, "E401", {"start": v(4.44, 2.27) * mm, "end": v(4.43, 2.3) * mm});
            skLineSegment(sketch, "E402", {"start": v(4.43, 2.3) * mm, "end": v(4.42, 2.35) * mm});
            skLineSegment(sketch, "E403", {"start": v(4.42, 2.35) * mm, "end": v(4.42, 2.37) * mm});
            skLineSegment(sketch, "E404", {"start": v(4.42, 2.37) * mm, "end": v(4.41, 2.4) * mm});
            skLineSegment(sketch, "E405", {"start": v(4.41, 2.4) * mm, "end": v(4.42, 2.4) * mm});
            skLineSegment(sketch, "E406", {"start": v(-4.87, 3.55) * mm, "end": v(-4.8, 3.47) * mm});
            skLineSegment(sketch, "E407", {"start": v(-4.8, 3.47) * mm, "end": v(-4.74, 3.4) * mm});
            skLineSegment(sketch, "E408", {"start": v(-4.74, 3.4) * mm, "end": v(-4.67, 3.3) * mm});
            skLineSegment(sketch, "E409", {"start": v(-4.67, 3.3) * mm, "end": v(-4.61, 3.23) * mm});
            skLineSegment(sketch, "E410", {"start": v(-4.61, 3.23) * mm, "end": v(-4.57, 3.16) * mm});
            skLineSegment(sketch, "E411", {"start": v(-4.57, 3.16) * mm, "end": v(-4.54, 3.12) * mm});
            skLineSegment(sketch, "E412", {"start": v(-4.54, 3.12) * mm, "end": v(-4.53, 3.05) * mm});
            skLineSegment(sketch, "E413", {"start": v(-4.53, 3.05) * mm, "end": v(-4.53, 2.95) * mm});
            skLineSegment(sketch, "E414", {"start": v(-4.53, 2.95) * mm, "end": v(-4.54, 2.88) * mm});
            skLineSegment(sketch, "E415", {"start": v(-4.54, 2.88) * mm, "end": v(-4.56, 2.8) * mm});
            skLineSegment(sketch, "E416", {"start": v(-4.56, 2.8) * mm, "end": v(-4.59, 2.74) * mm});
            skLineSegment(sketch, "E417", {"start": v(-4.59, 2.74) * mm, "end": v(-4.63, 2.7) * mm});
            skLineSegment(sketch, "E418", {"start": v(-4.63, 2.7) * mm, "end": v(-4.67, 2.68) * mm});
            skLineSegment(sketch, "E419", {"start": v(-4.67, 2.68) * mm, "end": v(-4.7, 2.67) * mm});
            skLineSegment(sketch, "E420", {"start": v(-4.7, 2.67) * mm, "end": v(-4.72, 2.67) * mm});
            skLineSegment(sketch, "E421", {"start": v(-4.72, 2.67) * mm, "end": v(-4.74, 2.67) * mm});
            skLineSegment(sketch, "E422", {"start": v(-4.74, 2.67) * mm, "end": v(-4.78, 2.7) * mm});
            skLineSegment(sketch, "E423", {"start": v(-4.78, 2.7) * mm, "end": v(-4.8, 2.74) * mm});
            skLineSegment(sketch, "E424", {"start": v(-4.8, 2.74) * mm, "end": v(-4.83, 2.78) * mm});
            skLineSegment(sketch, "E425", {"start": v(-4.83, 2.78) * mm, "end": v(-4.84, 2.83) * mm});
            skLineSegment(sketch, "E426", {"start": v(-4.84, 2.83) * mm, "end": v(-4.86, 2.9) * mm});
            skLineSegment(sketch, "E427", {"start": v(-4.86, 2.9) * mm, "end": v(-4.87, 2.95) * mm});
            skLineSegment(sketch, "E428", {"start": v(-4.87, 2.95) * mm, "end": v(-4.88, 3.02) * mm});
            skLineSegment(sketch, "E429", {"start": v(-4.88, 3.02) * mm, "end": v(-4.9, 3.09) * mm});
            skLineSegment(sketch, "E430", {"start": v(-4.9, 3.09) * mm, "end": v(-4.9, 3.16) * mm});
            skLineSegment(sketch, "E431", {"start": v(-4.9, 3.16) * mm, "end": v(-4.9, 3.26) * mm});
            skLineSegment(sketch, "E432", {"start": v(-4.9, 3.26) * mm, "end": v(-4.9, 3.34) * mm});
            skLineSegment(sketch, "E433", {"start": v(-4.9, 3.34) * mm, "end": v(-4.9, 3.42) * mm});
            skLineSegment(sketch, "E434", {"start": v(-4.9, 3.42) * mm, "end": v(-4.9, 3.5) * mm});
            skLineSegment(sketch, "E435", {"start": v(-4.9, 3.5) * mm, "end": v(-4.9, 3.54) * mm});
            skLineSegment(sketch, "E436", {"start": v(-4.9, 3.54) * mm, "end": v(-4.9, 3.55) * mm});
            skLineSegment(sketch, "E437", {"start": v(-4.9, 3.55) * mm, "end": v(-4.88, 3.55) * mm});
            skLineSegment(sketch, "E438", {"start": v(-4.87, 3.55) * mm, "end": v(-4.88, 3.55) * mm});
            skLineSegment(sketch, "E439", {"start": v(4.2, 3.18) * mm, "end": v(4.24, 3.26) * mm});
            skLineSegment(sketch, "E440", {"start": v(4.24, 3.26) * mm, "end": v(4.29, 3.32) * mm});
            skLineSegment(sketch, "E441", {"start": v(4.29, 3.32) * mm, "end": v(4.34, 3.4) * mm});
            skLineSegment(sketch, "E442", {"start": v(4.34, 3.4) * mm, "end": v(4.4, 3.45) * mm});
            skLineSegment(sketch, "E443", {"start": v(4.4, 3.45) * mm, "end": v(4.45, 3.52) * mm});
            skLineSegment(sketch, "E444", {"start": v(4.45, 3.52) * mm, "end": v(4.51, 3.6) * mm});
            skLineSegment(sketch, "E445", {"start": v(4.51, 3.6) * mm, "end": v(4.55, 3.64) * mm});
            skLineSegment(sketch, "E446", {"start": v(4.55, 3.64) * mm, "end": v(4.56, 3.65) * mm});
            skLineSegment(sketch, "E447", {"start": v(4.56, 3.65) * mm, "end": v(4.58, 3.62) * mm});
            skLineSegment(sketch, "E448", {"start": v(4.58, 3.62) * mm, "end": v(4.6, 3.57) * mm});
            skLineSegment(sketch, "E449", {"start": v(4.6, 3.57) * mm, "end": v(4.63, 3.52) * mm});
            skLineSegment(sketch, "E450", {"start": v(4.63, 3.52) * mm, "end": v(4.66, 3.44) * mm});
            skLineSegment(sketch, "E451", {"start": v(4.66, 3.44) * mm, "end": v(4.7, 3.36) * mm});
            skLineSegment(sketch, "E452", {"start": v(4.7, 3.36) * mm, "end": v(4.7, 3.24) * mm});
            skLineSegment(sketch, "E453", {"start": v(4.7, 3.24) * mm, "end": v(4.71, 3.14) * mm});
            skLineSegment(sketch, "E454", {"start": v(4.71, 3.14) * mm, "end": v(4.7, 3.05) * mm});
            skLineSegment(sketch, "E455", {"start": v(4.7, 3.05) * mm, "end": v(4.68, 2.96) * mm});
            skLineSegment(sketch, "E456", {"start": v(4.68, 2.96) * mm, "end": v(4.64, 2.9) * mm});
            skLineSegment(sketch, "E457", {"start": v(4.64, 2.9) * mm, "end": v(4.6, 2.84) * mm});
            skLineSegment(sketch, "E458", {"start": v(4.6, 2.84) * mm, "end": v(4.54, 2.8) * mm});
            skLineSegment(sketch, "E459", {"start": v(4.54, 2.8) * mm, "end": v(4.48, 2.77) * mm});
            skLineSegment(sketch, "E460", {"start": v(4.48, 2.77) * mm, "end": v(4.43, 2.77) * mm});
            skLineSegment(sketch, "E461", {"start": v(4.43, 2.77) * mm, "end": v(4.38, 2.79) * mm});
            skLineSegment(sketch, "E462", {"start": v(4.38, 2.79) * mm, "end": v(4.34, 2.82) * mm});
            skLineSegment(sketch, "E463", {"start": v(4.34, 2.82) * mm, "end": v(4.3, 2.88) * mm});
            skLineSegment(sketch, "E464", {"start": v(4.3, 2.88) * mm, "end": v(4.26, 2.93) * mm});
            skLineSegment(sketch, "E465", {"start": v(4.26, 2.93) * mm, "end": v(4.24, 2.99) * mm});
            skLineSegment(sketch, "E466", {"start": v(4.24, 2.99) * mm, "end": v(4.22, 3.04) * mm});
            skLineSegment(sketch, "E467", {"start": v(4.22, 3.04) * mm, "end": v(4.2, 3.1) * mm});
            skLineSegment(sketch, "E468", {"start": v(4.2, 3.1) * mm, "end": v(4.2, 3.15) * mm});
            skLineSegment(sketch, "E469", {"start": v(4.2, 3.15) * mm, "end": v(4.2, 3.18) * mm});
            skLineSegment(sketch, "E470", {"start": v(2.36, 0.86) * mm, "end": v(2.41, 0.94) * mm});
            skLineSegment(sketch, "E471", {"start": v(2.41, 0.94) * mm, "end": v(2.53, 1.11) * mm});
            skLineSegment(sketch, "E472", {"start": v(2.53, 1.11) * mm, "end": v(2.66, 1.29) * mm});
            skLineSegment(sketch, "E473", {"start": v(2.66, 1.29) * mm, "end": v(2.82, 1.5) * mm});
            skLineSegment(sketch, "E474", {"start": v(2.82, 1.5) * mm, "end": v(2.95, 1.68) * mm});
            skLineSegment(sketch, "E475", {"start": v(2.95, 1.68) * mm, "end": v(3.08, 1.84) * mm});
            skLineSegment(sketch, "E476", {"start": v(3.08, 1.84) * mm, "end": v(3.23, 2.03) * mm});
            skLineSegment(sketch, "E477", {"start": v(3.23, 2.03) * mm, "end": v(3.4, 2.25) * mm});
            skLineSegment(sketch, "E478", {"start": v(3.4, 2.25) * mm, "end": v(3.57, 2.46) * mm});
            skLineSegment(sketch, "E479", {"start": v(3.57, 2.46) * mm, "end": v(3.7, 2.62) * mm});
            skLineSegment(sketch, "E480", {"start": v(3.7, 2.62) * mm, "end": v(3.78, 2.7) * mm});
            skLineSegment(sketch, "E481", {"start": v(3.78, 2.7) * mm, "end": v(3.8, 2.71) * mm});
            skLineSegment(sketch, "E482", {"start": v(3.8, 2.71) * mm, "end": v(3.83, 2.71) * mm});
            skLineSegment(sketch, "E483", {"start": v(3.83, 2.71) * mm, "end": v(3.85, 2.7) * mm});
            skLineSegment(sketch, "E484", {"start": v(3.85, 2.7) * mm, "end": v(3.87, 2.58) * mm});
            skLineSegment(sketch, "E485", {"start": v(3.87, 2.58) * mm, "end": v(3.95, 2.26) * mm});
            skLineSegment(sketch, "E486", {"start": v(3.95, 2.26) * mm, "end": v(4.06, 2.01) * mm});
            skLineSegment(sketch, "E487", {"start": v(4.06, 2.01) * mm, "end": v(4.12, 1.86) * mm});
            skLineSegment(sketch, "E488", {"start": v(4.12, 1.86) * mm, "end": v(4.18, 1.72) * mm});
            skLineSegment(sketch, "E489", {"start": v(4.18, 1.72) * mm, "end": v(4.23, 1.6) * mm});
            skLineSegment(sketch, "E490", {"start": v(4.23, 1.6) * mm, "end": v(4.3, 1.5) * mm});
            skLineSegment(sketch, "E491", {"start": v(4.3, 1.5) * mm, "end": v(4.35, 1.43) * mm});
            skLineSegment(sketch, "E492", {"start": v(4.35, 1.43) * mm, "end": v(4.4, 1.37) * mm});
            skLineSegment(sketch, "E493", {"start": v(4.4, 1.37) * mm, "end": v(4.48, 1.3) * mm});
            skLineSegment(sketch, "E494", {"start": v(4.48, 1.3) * mm, "end": v(4.54, 1.25) * mm});
            skLineSegment(sketch, "E495", {"start": v(4.54, 1.25) * mm, "end": v(4.61, 1.22) * mm});
            skLineSegment(sketch, "E496", {"start": v(4.61, 1.22) * mm, "end": v(4.7, 1.2) * mm});
            skLineSegment(sketch, "E497", {"start": v(4.7, 1.2) * mm, "end": v(4.77, 1.2) * mm});
            skLineSegment(sketch, "E498", {"start": v(4.77, 1.2) * mm, "end": v(4.87, 1.22) * mm});
            skLineSegment(sketch, "E499", {"start": v(4.87, 1.22) * mm, "end": v(4.95, 1.26) * mm});
            skLineSegment(sketch, "E500", {"start": v(4.95, 1.26) * mm, "end": v(5, 1.32) * mm});
            skLineSegment(sketch, "E501", {"start": v(5, 1.32) * mm, "end": v(5.06, 1.37) * mm});
            skLineSegment(sketch, "E502", {"start": v(5.06, 1.37) * mm, "end": v(5.12, 1.46) * mm});
            skLineSegment(sketch, "E503", {"start": v(5.12, 1.46) * mm, "end": v(5.18, 1.56) * mm});
            skLineSegment(sketch, "E504", {"start": v(5.18, 1.56) * mm, "end": v(5.22, 1.66) * mm});
            skLineSegment(sketch, "E505", {"start": v(5.22, 1.66) * mm, "end": v(5.25, 1.77) * mm});
            skLineSegment(sketch, "E506", {"start": v(5.25, 1.77) * mm, "end": v(5.26, 1.88) * mm});
            skLineSegment(sketch, "E507", {"start": v(5.26, 1.88) * mm, "end": v(5.27, 1.98) * mm});
            skLineSegment(sketch, "E508", {"start": v(5.27, 1.98) * mm, "end": v(5.27, 2.09) * mm});
            skLineSegment(sketch, "E509", {"start": v(5.27, 2.09) * mm, "end": v(5.27, 2.2) * mm});
            skLineSegment(sketch, "E510", {"start": v(5.27, 2.2) * mm, "end": v(5.27, 2.32) * mm});
            skLineSegment(sketch, "E511", {"start": v(5.27, 2.32) * mm, "end": v(5.27, 2.45) * mm});
            skLineSegment(sketch, "E512", {"start": v(5.27, 2.45) * mm, "end": v(5.26, 2.56) * mm});
            skLineSegment(sketch, "E513", {"start": v(5.26, 2.56) * mm, "end": v(5.25, 2.62) * mm});
            skLineSegment(sketch, "E514", {"start": v(5.25, 2.62) * mm, "end": v(5.24, 2.81) * mm});
            skLineSegment(sketch, "E515", {"start": v(5.24, 2.81) * mm, "end": v(5.22, 2.95) * mm});
            skLineSegment(sketch, "E516", {"start": v(5.22, 2.95) * mm, "end": v(5.2, 3.07) * mm});
            skLineSegment(sketch, "E517", {"start": v(5.2, 3.07) * mm, "end": v(5.17, 3.22) * mm});
            skLineSegment(sketch, "E518", {"start": v(5.17, 3.22) * mm, "end": v(5.14, 3.35) * mm});
            skLineSegment(sketch, "E519", {"start": v(5.14, 3.35) * mm, "end": v(5.1, 3.5) * mm});
            skLineSegment(sketch, "E520", {"start": v(5.1, 3.5) * mm, "end": v(5.07, 3.64) * mm});
            skLineSegment(sketch, "E521", {"start": v(5.07, 3.64) * mm, "end": v(5.04, 3.74) * mm});
            skLineSegment(sketch, "E522", {"start": v(5.04, 3.74) * mm, "end": v(5, 3.88) * mm});
            skLineSegment(sketch, "E523", {"start": v(5, 3.88) * mm, "end": v(4.96, 3.95) * mm});
            skLineSegment(sketch, "E524", {"start": v(4.96, 3.95) * mm, "end": v(4.94, 4) * mm});
            skLineSegment(sketch, "E525", {"start": v(4.94, 4) * mm, "end": v(4.93, 4.05) * mm});
            skLineSegment(sketch, "E526", {"start": v(4.93, 4.05) * mm, "end": v(4.94, 4.08) * mm});
            skLineSegment(sketch, "E527", {"start": v(4.94, 4.08) * mm, "end": v(4.95, 4.1) * mm});
            skLineSegment(sketch, "E528", {"start": v(4.95, 4.1) * mm, "end": v(4.97, 4.14) * mm});
            skLineSegment(sketch, "E529", {"start": v(4.97, 4.14) * mm, "end": v(5, 4.18) * mm});
            skLineSegment(sketch, "E530", {"start": v(5, 4.18) * mm, "end": v(5.05, 4.24) * mm});
            skLineSegment(sketch, "E531", {"start": v(5.05, 4.24) * mm, "end": v(5.12, 4.32) * mm});
            skLineSegment(sketch, "E532", {"start": v(5.12, 4.32) * mm, "end": v(5.18, 4.4) * mm});
            skLineSegment(sketch, "E533", {"start": v(5.18, 4.4) * mm, "end": v(5.23, 4.45) * mm});
            skLineSegment(sketch, "E534", {"start": v(5.23, 4.45) * mm, "end": v(5.32, 4.55) * mm});
            skLineSegment(sketch, "E535", {"start": v(5.32, 4.55) * mm, "end": v(5.4, 4.63) * mm});
            skLineSegment(sketch, "E536", {"start": v(5.4, 4.63) * mm, "end": v(5.48, 4.73) * mm});
            skLineSegment(sketch, "E537", {"start": v(5.48, 4.73) * mm, "end": v(5.57, 4.84) * mm});
            skLineSegment(sketch, "E538", {"start": v(5.57, 4.84) * mm, "end": v(5.62, 4.9) * mm});
            skLineSegment(sketch, "E539", {"start": v(5.62, 4.9) * mm, "end": v(5.7, 4.98) * mm});
            skLineSegment(sketch, "E540", {"start": v(5.7, 4.98) * mm, "end": v(5.77, 5.08) * mm});
            skLineSegment(sketch, "E541", {"start": v(5.77, 5.08) * mm, "end": v(5.83, 5.15) * mm});
            skLineSegment(sketch, "E542", {"start": v(5.83, 5.15) * mm, "end": v(5.93, 5.26) * mm});
            skLineSegment(sketch, "E543", {"start": v(5.93, 5.26) * mm, "end": v(6.01, 5.36) * mm});
            skLineSegment(sketch, "E544", {"start": v(6.01, 5.36) * mm, "end": v(6.11, 5.47) * mm});
            skLineSegment(sketch, "E545", {"start": v(6.11, 5.47) * mm, "end": v(6.2, 5.56) * mm});
            skLineSegment(sketch, "E546", {"start": v(6.2, 5.56) * mm, "end": v(6.27, 5.64) * mm});
            skLineSegment(sketch, "E547", {"start": v(6.27, 5.64) * mm, "end": v(6.3, 5.68) * mm});
            skLineSegment(sketch, "E548", {"start": v(6.3, 5.68) * mm, "end": v(6.36, 5.75) * mm});
            skLineSegment(sketch, "E549", {"start": v(6.36, 5.75) * mm, "end": v(6.45, 5.85) * mm});
            skLineSegment(sketch, "E550", {"start": v(6.45, 5.85) * mm, "end": v(6.53, 5.94) * mm});
            skLineSegment(sketch, "E551", {"start": v(6.53, 5.94) * mm, "end": v(6.6, 6.02) * mm});
            skLineSegment(sketch, "E552", {"start": v(6.6, 6.02) * mm, "end": v(6.68, 6.1) * mm});
            skLineSegment(sketch, "E553", {"start": v(6.68, 6.1) * mm, "end": v(6.78, 6.2) * mm});
            skLineSegment(sketch, "E554", {"start": v(6.78, 6.2) * mm, "end": v(6.87, 6.3) * mm});
            skLineSegment(sketch, "E555", {"start": v(6.87, 6.3) * mm, "end": v(6.94, 6.39) * mm});
            skLineSegment(sketch, "E556", {"start": v(6.94, 6.39) * mm, "end": v(7.05, 6.5) * mm});
            skLineSegment(sketch, "E557", {"start": v(7.05, 6.5) * mm, "end": v(7.16, 6.63) * mm});
            skLineSegment(sketch, "E558", {"start": v(7.16, 6.63) * mm, "end": v(7.3, 6.79) * mm});
            skLineSegment(sketch, "E559", {"start": v(7.3, 6.79) * mm, "end": v(7.43, 6.93) * mm});
            skLineSegment(sketch, "E560", {"start": v(7.43, 6.93) * mm, "end": v(7.5, 7) * mm});
            skLineSegment(sketch, "E561", {"start": v(7.5, 7) * mm, "end": v(7.58, 7.08) * mm});
            skLineSegment(sketch, "E562", {"start": v(7.58, 7.08) * mm, "end": v(7.62, 7.12) * mm});
            skLineSegment(sketch, "E563", {"start": v(7.62, 7.12) * mm, "end": v(7.64, 7.14) * mm});
            skLineSegment(sketch, "E564", {"start": v(7.64, 7.14) * mm, "end": v(7.65, 7.15) * mm});
            skLineSegment(sketch, "E565", {"start": v(7.65, 7.15) * mm, "end": v(7.66, 7.15) * mm});
            skLineSegment(sketch, "E566", {"start": v(7.66, 7.15) * mm, "end": v(7.67, 7.13) * mm});
            skLineSegment(sketch, "E567", {"start": v(7.67, 7.13) * mm, "end": v(7.74, 7.02) * mm});
            skLineSegment(sketch, "E568", {"start": v(7.74, 7.02) * mm, "end": v(7.83, 6.87) * mm});
            skLineSegment(sketch, "E569", {"start": v(7.83, 6.87) * mm, "end": v(7.9, 6.74) * mm});
            skLineSegment(sketch, "E570", {"start": v(7.9, 6.74) * mm, "end": v(7.96, 6.59) * mm});
            skLineSegment(sketch, "E571", {"start": v(7.96, 6.59) * mm, "end": v(8.03, 6.43) * mm});
            skLineSegment(sketch, "E572", {"start": v(8.03, 6.43) * mm, "end": v(8.08, 6.28) * mm});
            skLineSegment(sketch, "E573", {"start": v(8.08, 6.28) * mm, "end": v(8.13, 6.17) * mm});
            skLineSegment(sketch, "E574", {"start": v(8.13, 6.17) * mm, "end": v(8.18, 6.04) * mm});
            skLineSegment(sketch, "E575", {"start": v(8.18, 6.04) * mm, "end": v(8.22, 5.97) * mm});
            skLineSegment(sketch, "E576", {"start": v(8.22, 5.97) * mm, "end": v(8.25, 5.85) * mm});
            skLineSegment(sketch, "E577", {"start": v(8.25, 5.85) * mm, "end": v(8.27, 5.73) * mm});
            skLineSegment(sketch, "E578", {"start": v(8.27, 5.73) * mm, "end": v(8.3, 5.61) * mm});
            skLineSegment(sketch, "E579", {"start": v(8.3, 5.61) * mm, "end": v(8.36, 5.44) * mm});
            skLineSegment(sketch, "E580", {"start": v(8.36, 5.44) * mm, "end": v(8.4, 5.3) * mm});
            skLineSegment(sketch, "E581", {"start": v(8.4, 5.3) * mm, "end": v(8.43, 5.14) * mm});
            skLineSegment(sketch, "E582", {"start": v(8.43, 5.14) * mm, "end": v(8.45, 5.02) * mm});
            skLineSegment(sketch, "E583", {"start": v(8.45, 5.02) * mm, "end": v(8.46, 4.9) * mm});
            skLineSegment(sketch, "E584", {"start": v(8.46, 4.9) * mm, "end": v(8.5, 4.74) * mm});
            skLineSegment(sketch, "E585", {"start": v(8.5, 4.74) * mm, "end": v(8.53, 4.62) * mm});
            skLineSegment(sketch, "E586", {"start": v(8.53, 4.62) * mm, "end": v(8.54, 4.55) * mm});
            skLineSegment(sketch, "E587", {"start": v(8.54, 4.55) * mm, "end": v(8.56, 4.43) * mm});
            skLineSegment(sketch, "E588", {"start": v(8.56, 4.43) * mm, "end": v(8.56, 4.31) * mm});
            skLineSegment(sketch, "E589", {"start": v(8.56, 4.31) * mm, "end": v(8.57, 4.2) * mm});
            skLineSegment(sketch, "E590", {"start": v(8.57, 4.2) * mm, "end": v(8.57, 4.1) * mm});
            skLineSegment(sketch, "E591", {"start": v(8.57, 4.1) * mm, "end": v(8.57, 3.97) * mm});
            skLineSegment(sketch, "E592", {"start": v(8.57, 3.97) * mm, "end": v(8.57, 3.84) * mm});
            skLineSegment(sketch, "E593", {"start": v(8.57, 3.84) * mm, "end": v(8.58, 3.73) * mm});
            skLineSegment(sketch, "E594", {"start": v(8.58, 3.73) * mm, "end": v(8.58, 3.65) * mm});
            skLineSegment(sketch, "E595", {"start": v(8.58, 3.65) * mm, "end": v(8.57, 3.54) * mm});
            skLineSegment(sketch, "E596", {"start": v(8.57, 3.54) * mm, "end": v(8.57, 3.43) * mm});
            skLineSegment(sketch, "E597", {"start": v(8.57, 3.43) * mm, "end": v(8.57, 3.3) * mm});
            skLineSegment(sketch, "E598", {"start": v(8.57, 3.3) * mm, "end": v(8.56, 3.22) * mm});
            skLineSegment(sketch, "E599", {"start": v(8.56, 3.22) * mm, "end": v(8.54, 3.08) * mm});
            skLineSegment(sketch, "E600", {"start": v(8.54, 3.08) * mm, "end": v(8.53, 2.97) * mm});
            skLineSegment(sketch, "E601", {"start": v(8.53, 2.97) * mm, "end": v(8.5, 2.87) * mm});
            skLineSegment(sketch, "E602", {"start": v(8.5, 2.87) * mm, "end": v(8.5, 2.75) * mm});
            skLineSegment(sketch, "E603", {"start": v(8.5, 2.75) * mm, "end": v(8.47, 2.65) * mm});
            skLineSegment(sketch, "E604", {"start": v(8.47, 2.65) * mm, "end": v(8.43, 2.5) * mm});
            skLineSegment(sketch, "E605", {"start": v(8.43, 2.5) * mm, "end": v(8.4, 2.4) * mm});
            skLineSegment(sketch, "E606", {"start": v(8.4, 2.4) * mm, "end": v(8.38, 2.3) * mm});
            skLineSegment(sketch, "E607", {"start": v(8.38, 2.3) * mm, "end": v(8.34, 2.2) * mm});
            skLineSegment(sketch, "E608", {"start": v(8.34, 2.2) * mm, "end": v(8.31, 2.1) * mm});
            skLineSegment(sketch, "E609", {"start": v(8.31, 2.1) * mm, "end": v(8.27, 1.98) * mm});
            skLineSegment(sketch, "E610", {"start": v(8.27, 1.98) * mm, "end": v(8.23, 1.9) * mm});
            skLineSegment(sketch, "E611", {"start": v(8.23, 1.9) * mm, "end": v(8.2, 1.82) * mm});
            skLineSegment(sketch, "E612", {"start": v(8.2, 1.82) * mm, "end": v(8.13, 1.66) * mm});
            skLineSegment(sketch, "E613", {"start": v(8.13, 1.66) * mm, "end": v(8.1, 1.58) * mm});
            skLineSegment(sketch, "E614", {"start": v(8.1, 1.58) * mm, "end": v(8.04, 1.5) * mm});
            skLineSegment(sketch, "E615", {"start": v(8.04, 1.5) * mm, "end": v(8.02, 1.44) * mm});
            skLineSegment(sketch, "E616", {"start": v(8.02, 1.44) * mm, "end": v(7.96, 1.34) * mm});
            skLineSegment(sketch, "E617", {"start": v(7.96, 1.34) * mm, "end": v(7.91, 1.26) * mm});
            skLineSegment(sketch, "E618", {"start": v(7.91, 1.26) * mm, "end": v(7.85, 1.18) * mm});
            skLineSegment(sketch, "E619", {"start": v(7.85, 1.18) * mm, "end": v(7.78, 1.08) * mm});
            skLineSegment(sketch, "E620", {"start": v(7.78, 1.08) * mm, "end": v(7.74, 1.02) * mm});
            skLineSegment(sketch, "E621", {"start": v(7.74, 1.02) * mm, "end": v(7.66, 0.92) * mm});
            skLineSegment(sketch, "E622", {"start": v(7.66, 0.92) * mm, "end": v(7.6, 0.83) * mm});
            skLineSegment(sketch, "E623", {"start": v(7.6, 0.83) * mm, "end": v(7.55, 0.78) * mm});
            skLineSegment(sketch, "E624", {"start": v(7.55, 0.78) * mm, "end": v(7.5, 0.72) * mm});
            skLineSegment(sketch, "E625", {"start": v(7.5, 0.72) * mm, "end": v(7.43, 0.65) * mm});
            skLineSegment(sketch, "E626", {"start": v(7.43, 0.65) * mm, "end": v(7.35, 0.58) * mm});
            skLineSegment(sketch, "E627", {"start": v(7.35, 0.58) * mm, "end": v(7.27, 0.5) * mm});
            skLineSegment(sketch, "E628", {"start": v(7.27, 0.5) * mm, "end": v(7.2, 0.45) * mm});
            skLineSegment(sketch, "E629", {"start": v(7.2, 0.45) * mm, "end": v(7.15, 0.4) * mm});
            skLineSegment(sketch, "E630", {"start": v(7.15, 0.4) * mm, "end": v(7.06, 0.34) * mm});
            skLineSegment(sketch, "E631", {"start": v(7.06, 0.34) * mm, "end": v(6.98, 0.28) * mm});
            skLineSegment(sketch, "E632", {"start": v(6.98, 0.28) * mm, "end": v(6.9, 0.23) * mm});
            skLineSegment(sketch, "E633", {"start": v(6.9, 0.23) * mm, "end": v(6.8, 0.17) * mm});
            skLineSegment(sketch, "E634", {"start": v(6.8, 0.17) * mm, "end": v(6.7, 0.1) * mm});
            skLineSegment(sketch, "E635", {"start": v(6.7, 0.1) * mm, "end": v(6.6, 0.05) * mm});
            skLineSegment(sketch, "E636", {"start": v(6.6, 0.05) * mm, "end": v(6.5, 0.02) * mm});
            skLineSegment(sketch, "E637", {"start": v(6.5, 0.02) * mm, "end": v(6.43, -0.01) * mm});
            skLineSegment(sketch, "E638", {"start": v(6.43, -0.01) * mm, "end": v(6.32, -0.06) * mm});
            skLineSegment(sketch, "E639", {"start": v(6.32, -0.06) * mm, "end": v(6.2, -0.1) * mm});
            skLineSegment(sketch, "E640", {"start": v(6.2, -0.1) * mm, "end": v(6.1, -0.14) * mm});
            skLineSegment(sketch, "E641", {"start": v(6.1, -0.14) * mm, "end": v(6, -0.16) * mm});
            skLineSegment(sketch, "E642", {"start": v(6, -0.16) * mm, "end": v(5.92, -0.18) * mm});
            skLineSegment(sketch, "E643", {"start": v(5.92, -0.18) * mm, "end": v(5.81, -0.2) * mm});
            skLineSegment(sketch, "E644", {"start": v(5.81, -0.2) * mm, "end": v(5.7, -0.22) * mm});
            skLineSegment(sketch, "E645", {"start": v(5.7, -0.22) * mm, "end": v(5.58, -0.24) * mm});
            skLineSegment(sketch, "E646", {"start": v(5.58, -0.24) * mm, "end": v(5.38, -0.26) * mm});
            skLineSegment(sketch, "E647", {"start": v(5.38, -0.26) * mm, "end": v(5.28, -0.27) * mm});
            skLineSegment(sketch, "E648", {"start": v(5.28, -0.27) * mm, "end": v(5.16, -0.27) * mm});
            skLineSegment(sketch, "E649", {"start": v(5.16, -0.27) * mm, "end": v(5.04, -0.27) * mm});
            skLineSegment(sketch, "E650", {"start": v(5.04, -0.27) * mm, "end": v(4.94, -0.27) * mm});
            skLineSegment(sketch, "E651", {"start": v(4.94, -0.27) * mm, "end": v(4.85, -0.26) * mm});
            skLineSegment(sketch, "E652", {"start": v(4.85, -0.26) * mm, "end": v(4.64, -0.24) * mm});
            skLineSegment(sketch, "E653", {"start": v(4.64, -0.24) * mm, "end": v(4.52, -0.23) * mm});
            skLineSegment(sketch, "E654", {"start": v(4.52, -0.23) * mm, "end": v(4.36, -0.2) * mm});
            skLineSegment(sketch, "E655", {"start": v(4.36, -0.2) * mm, "end": v(4.2, -0.17) * mm});
            skLineSegment(sketch, "E656", {"start": v(4.2, -0.17) * mm, "end": v(4.04, -0.12) * mm});
            skLineSegment(sketch, "E657", {"start": v(4.04, -0.12) * mm, "end": v(3.85, -0.07) * mm});
            skLineSegment(sketch, "E658", {"start": v(3.85, -0.07) * mm, "end": v(3.71, -0.02) * mm});
            skLineSegment(sketch, "E659", {"start": v(3.71, -0.02) * mm, "end": v(3.62, 0.02) * mm});
            skLineSegment(sketch, "E660", {"start": v(3.62, 0.02) * mm, "end": v(3.39, 0.1) * mm});
            skLineSegment(sketch, "E661", {"start": v(3.39, 0.1) * mm, "end": v(3.24, 0.18) * mm});
            skLineSegment(sketch, "E662", {"start": v(3.24, 0.18) * mm, "end": v(3.07, 0.27) * mm});
            skLineSegment(sketch, "E663", {"start": v(3.07, 0.27) * mm, "end": v(2.89, 0.38) * mm});
            skLineSegment(sketch, "E664", {"start": v(2.89, 0.38) * mm, "end": v(2.74, 0.49) * mm});
            skLineSegment(sketch, "E665", {"start": v(2.74, 0.49) * mm, "end": v(2.63, 0.58) * mm});
            skLineSegment(sketch, "E666", {"start": v(2.63, 0.58) * mm, "end": v(2.52, 0.68) * mm});
            skLineSegment(sketch, "E667", {"start": v(2.52, 0.68) * mm, "end": v(2.44, 0.76) * mm});
            skLineSegment(sketch, "E668", {"start": v(2.44, 0.76) * mm, "end": v(2.38, 0.82) * mm});
            skLineSegment(sketch, "E669", {"start": v(2.38, 0.82) * mm, "end": v(2.36, 0.84) * mm});
            skLineSegment(sketch, "E670", {"start": v(2.36, 0.84) * mm, "end": v(2.35, 0.85) * mm});
            skLineSegment(sketch, "E671", {"start": v(2.35, 0.85) * mm, "end": v(2.35, 0.86) * mm});
            skLineSegment(sketch, "E672", {"start": v(2.35, 0.86) * mm, "end": v(2.36, 0.86) * mm});
            skSolve(sketch);
        }
        {
            var Q0;
            Q0 = qSketchRegion(id + "F2", true);
            extrude(context, id + "F3", {"entities" : qUnion([Q0]), "operationType" : NewBodyOperationType.REMOVE, "depth" : 25 * mm});
        }
        {
            var Q0;
            Q0=qCreatedBy(makeId("Front.planeOp"),FACE);
            var sketch = newSketch(context, id + "F4", { "sketchPlane" : qUnion([Q0])});
            skLineSegment(sketch, "E673", {"start": v(-4.84, 2.37) * mm, "end": v(-4.8, 2.36) * mm});
            skLineSegment(sketch, "E674", {"start": v(-4.8, 2.36) * mm, "end": v(-4.77, 2.35) * mm});
            skLineSegment(sketch, "E675", {"start": v(-4.77, 2.35) * mm, "end": v(-4.73, 2.34) * mm});
            skLineSegment(sketch, "E676", {"start": v(-4.73, 2.34) * mm, "end": v(-4.68, 2.34) * mm});
            skLineSegment(sketch, "E677", {"start": v(-4.68, 2.34) * mm, "end": v(-4.65, 2.34) * mm});
            skLineSegment(sketch, "E678", {"start": v(-4.65, 2.34) * mm, "end": v(-4.61, 2.34) * mm});
            skLineSegment(sketch, "E679", {"start": v(-4.61, 2.34) * mm, "end": v(-4.58, 2.34) * mm});
            skLineSegment(sketch, "E680", {"start": v(-4.58, 2.34) * mm, "end": v(-4.54, 2.34) * mm});
            skLineSegment(sketch, "E681", {"start": v(-4.54, 2.34) * mm, "end": v(-4.5, 2.35) * mm});
            skLineSegment(sketch, "E682", {"start": v(-4.5, 2.35) * mm, "end": v(-4.45, 2.36) * mm});
            skLineSegment(sketch, "E683", {"start": v(-4.45, 2.36) * mm, "end": v(-4.42, 2.37) * mm});
            skLineSegment(sketch, "E684", {"start": v(-4.42, 2.37) * mm, "end": v(-4.4, 2.38) * mm});
            skLineSegment(sketch, "E685", {"start": v(-4.4, 2.38) * mm, "end": v(-4.39, 2.38) * mm});
            skLineSegment(sketch, "E686", {"start": v(-4.39, 2.38) * mm, "end": v(-4.38, 2.28) * mm});
            skLineSegment(sketch, "E687", {"start": v(-4.38, 2.28) * mm, "end": v(-4.38, 2.21) * mm});
            skLineSegment(sketch, "E688", {"start": v(-4.38, 2.21) * mm, "end": v(-4.38, 2.16) * mm});
            skLineSegment(sketch, "E689", {"start": v(-4.38, 2.16) * mm, "end": v(-4.4, 2) * mm});
            skLineSegment(sketch, "E690", {"start": v(-4.4, 2) * mm, "end": v(-4.4, 1.96) * mm});
            skLineSegment(sketch, "E691", {"start": v(-4.4, 1.96) * mm, "end": v(-4.42, 1.9) * mm});
            skLineSegment(sketch, "E692", {"start": v(-4.42, 1.9) * mm, "end": v(-4.43, 1.86) * mm});
            skLineSegment(sketch, "E693", {"start": v(-4.43, 1.86) * mm, "end": v(-4.45, 1.82) * mm});
            skLineSegment(sketch, "E694", {"start": v(-4.45, 1.82) * mm, "end": v(-4.47, 1.78) * mm});
            skLineSegment(sketch, "E695", {"start": v(-4.47, 1.78) * mm, "end": v(-4.5, 1.74) * mm});
            skLineSegment(sketch, "E696", {"start": v(-4.5, 1.74) * mm, "end": v(-4.52, 1.73) * mm});
            skLineSegment(sketch, "E697", {"start": v(-4.52, 1.73) * mm, "end": v(-4.55, 1.71) * mm});
            skLineSegment(sketch, "E698", {"start": v(-4.55, 1.71) * mm, "end": v(-4.56, 1.7) * mm});
            skLineSegment(sketch, "E699", {"start": v(-4.56, 1.7) * mm, "end": v(-4.59, 1.7) * mm});
            skLineSegment(sketch, "E700", {"start": v(-4.59, 1.7) * mm, "end": v(-4.61, 1.7) * mm});
            skLineSegment(sketch, "E701", {"start": v(-4.61, 1.7) * mm, "end": v(-4.64, 1.7) * mm});
            skLineSegment(sketch, "E702", {"start": v(-4.64, 1.7) * mm, "end": v(-4.65, 1.72) * mm});
            skLineSegment(sketch, "E703", {"start": v(-4.65, 1.72) * mm, "end": v(-4.68, 1.73) * mm});
            skLineSegment(sketch, "E704", {"start": v(-4.68, 1.73) * mm, "end": v(-4.7, 1.75) * mm});
            skLineSegment(sketch, "E705", {"start": v(-4.7, 1.75) * mm, "end": v(-4.72, 1.77) * mm});
            skLineSegment(sketch, "E706", {"start": v(-4.72, 1.77) * mm, "end": v(-4.73, 1.8) * mm});
            skLineSegment(sketch, "E707", {"start": v(-4.73, 1.8) * mm, "end": v(-4.75, 1.82) * mm});
            skLineSegment(sketch, "E708", {"start": v(-4.75, 1.82) * mm, "end": v(-4.76, 1.85) * mm});
            skLineSegment(sketch, "E709", {"start": v(-4.76, 1.85) * mm, "end": v(-4.78, 1.89) * mm});
            skLineSegment(sketch, "E710", {"start": v(-4.78, 1.89) * mm, "end": v(-4.79, 1.92) * mm});
            skLineSegment(sketch, "E711", {"start": v(-4.79, 1.92) * mm, "end": v(-4.79, 1.94) * mm});
            skLineSegment(sketch, "E712", {"start": v(-4.79, 1.94) * mm, "end": v(-4.79, 1.96) * mm});
            skPoint(sketch, "E712.endSnap0", {"position": v(-4.79, 1.93) * mm});
            skLineSegment(sketch, "E713", {"start": v(-4.79, 1.96) * mm, "end": v(-4.8, 2) * mm});
            skLineSegment(sketch, "E714", {"start": v(-4.8, 2) * mm, "end": v(-4.8, 2.04) * mm});
            skLineSegment(sketch, "E715", {"start": v(-4.8, 2.04) * mm, "end": v(-4.8, 2.08) * mm});
            skLineSegment(sketch, "E716", {"start": v(-4.8, 2.08) * mm, "end": v(-4.82, 2.13) * mm});
            skLineSegment(sketch, "E717", {"start": v(-4.82, 2.13) * mm, "end": v(-4.82, 2.16) * mm});
            skLineSegment(sketch, "E718", {"start": v(-4.82, 2.16) * mm, "end": v(-4.83, 2.2) * mm});
            skLineSegment(sketch, "E719", {"start": v(-4.83, 2.2) * mm, "end": v(-4.83, 2.27) * mm});
            skLineSegment(sketch, "E720", {"start": v(-4.83, 2.27) * mm, "end": v(-4.84, 2.33) * mm});
            skLineSegment(sketch, "E721", {"start": v(-4.84, 2.33) * mm, "end": v(-4.84, 2.36) * mm});
            skLineSegment(sketch, "E722", {"start": v(-4.84, 2.36) * mm, "end": v(-4.85, 2.37) * mm});
            skLineSegment(sketch, "E723", {"start": v(-4.85, 2.37) * mm, "end": v(-4.84, 2.37) * mm});
            skSolve(sketch);
        }
        {
            var Q0;
            Q0 = qSketchRegion(id + "F4", true);
            extrude(context, id + "F5", {"entities" : qUnion([Q0]), "operationType" : NewBodyOperationType.REMOVE, "depth" : 25 * mm});
        }
        {
            var Q0;
            Q0=qCreatedBy(makeId("Front.planeOp"),FACE);
            var sketch = newSketch(context, id + "F6", { "sketchPlane" : qUnion([Q0])});
            skLineSegment(sketch, "E724", {"start": v(-10, -0.14) * mm, "end": v(-9.76, -0.37) * mm});
            skLineSegment(sketch, "E725", {"start": v(-9.76, -0.37) * mm, "end": v(-9.38, -0.73) * mm});
            skLineSegment(sketch, "E726", {"start": v(-9.38, -0.73) * mm, "end": v(-8.96, -1.06) * mm});
            skLineSegment(sketch, "E727", {"start": v(-8.96, -1.06) * mm, "end": v(-8.62, -1.3) * mm});
            skLineSegment(sketch, "E728", {"start": v(-8.62, -1.3) * mm, "end": v(-8.3, -1.52) * mm});
            skLineSegment(sketch, "E729", {"start": v(-8.3, -1.52) * mm, "end": v(-8.14, -1.61) * mm});
            skLineSegment(sketch, "E730", {"start": v(-8.14, -1.61) * mm, "end": v(-8.07, -1.65) * mm});
            skLineSegment(sketch, "E731", {"start": v(-8.07, -1.65) * mm, "end": v(-8.05, -1.74) * mm});
            skLineSegment(sketch, "E732", {"start": v(-8.05, -1.74) * mm, "end": v(-8.05, -2) * mm});
            skLineSegment(sketch, "E733", {"start": v(-8.05, -2) * mm, "end": v(-8.05, -2.51) * mm});
            skLineSegment(sketch, "E734", {"start": v(-8.05, -2.51) * mm, "end": v(-8.05, -3.11) * mm});
            skLineSegment(sketch, "E735", {"start": v(-8.05, -3.11) * mm, "end": v(-8.05, -3.67) * mm});
            skLineSegment(sketch, "E736", {"start": v(-8.05, -3.67) * mm, "end": v(-8.05, -4) * mm});
            skLineSegment(sketch, "E737", {"start": v(-8.05, -4) * mm, "end": v(-8.05, -4.36) * mm});
            skLineSegment(sketch, "E738", {"start": v(-8.05, -4.36) * mm, "end": v(-8.05, -4.57) * mm});
            skLineSegment(sketch, "E739", {"start": v(-8.05, -4.57) * mm, "end": v(-8.05, -4.65) * mm});
            skLineSegment(sketch, "E740", {"start": v(-8.05, -4.65) * mm, "end": v(-8.1, -4.61) * mm});
            skLineSegment(sketch, "E741", {"start": v(-8.1, -4.61) * mm, "end": v(-8.22, -4.47) * mm});
            skLineSegment(sketch, "E742", {"start": v(-8.22, -4.47) * mm, "end": v(-8.35, -4.32) * mm});
            skLineSegment(sketch, "E743", {"start": v(-8.35, -4.32) * mm, "end": v(-8.5, -4.1) * mm});
            skLineSegment(sketch, "E744", {"start": v(-8.5, -4.1) * mm, "end": v(-8.68, -3.85) * mm});
            skLineSegment(sketch, "E745", {"start": v(-8.68, -3.85) * mm, "end": v(-8.87, -3.54) * mm});
            skLineSegment(sketch, "E746", {"start": v(-8.87, -3.54) * mm, "end": v(-9.03, -3.25) * mm});
            skLineSegment(sketch, "E747", {"start": v(-9.03, -3.25) * mm, "end": v(-9.26, -2.8) * mm});
            skLineSegment(sketch, "E748", {"start": v(-9.26, -2.8) * mm, "end": v(-9.4, -2.44) * mm});
            skLineSegment(sketch, "E749", {"start": v(-9.4, -2.44) * mm, "end": v(-9.53, -2.15) * mm});
            skLineSegment(sketch, "E750", {"start": v(-9.53, -2.15) * mm, "end": v(-9.62, -1.85) * mm});
            skLineSegment(sketch, "E751", {"start": v(-9.62, -1.85) * mm, "end": v(-9.72, -1.56) * mm});
            skLineSegment(sketch, "E752", {"start": v(-9.72, -1.56) * mm, "end": v(-9.8, -1.3) * mm});
            skLineSegment(sketch, "E753", {"start": v(-9.8, -1.3) * mm, "end": v(-9.84, -1.1) * mm});
            skLineSegment(sketch, "E754", {"start": v(-9.84, -1.1) * mm, "end": v(-9.9, -0.87) * mm});
            skLineSegment(sketch, "E755", {"start": v(-9.9, -0.87) * mm, "end": v(-9.96, -0.64) * mm});
            skLineSegment(sketch, "E756", {"start": v(-9.96, -0.64) * mm, "end": v(-10, -0.45) * mm});
            skLineSegment(sketch, "E757", {"start": v(-10, -0.45) * mm, "end": v(-10.04, -0.32) * mm});
            skLineSegment(sketch, "E758", {"start": v(-10.04, -0.32) * mm, "end": v(-10.04, -0.24) * mm});
            skLineSegment(sketch, "E759", {"start": v(-10.04, -0.24) * mm, "end": v(-10.04, -0.18) * mm});
            skLineSegment(sketch, "E760", {"start": v(-10.04, -0.18) * mm, "end": v(-10.02, -0.14) * mm});
            skLineSegment(sketch, "E761", {"start": v(-10.02, -0.14) * mm, "end": v(-10, -0.14) * mm});
            skLineSegment(sketch, "E762", {"start": v(-7.52, -1.96) * mm, "end": v(-7.57, -2.08) * mm});
            skLineSegment(sketch, "E763", {"start": v(-7.57, -2.08) * mm, "end": v(-7.57, -2.33) * mm});
            skLineSegment(sketch, "E764", {"start": v(-7.57, -2.33) * mm, "end": v(-7.57, -3.3) * mm});
            skLineSegment(sketch, "E765", {"start": v(-7.57, -3.3) * mm, "end": v(-7.57, -3.99) * mm});
            skLineSegment(sketch, "E766", {"start": v(-7.57, -3.99) * mm, "end": v(-7.57, -4.54) * mm});
            skLineSegment(sketch, "E767", {"start": v(-7.57, -4.54) * mm, "end": v(-7.57, -4.97) * mm});
            skLineSegment(sketch, "E768", {"start": v(-7.57, -4.97) * mm, "end": v(-7.57, -5.1) * mm});
            skLineSegment(sketch, "E769", {"start": v(-7.57, -5.1) * mm, "end": v(-7.54, -5.2) * mm});
            skLineSegment(sketch, "E770", {"start": v(-7.54, -5.2) * mm, "end": v(-7.38, -5.36) * mm});
            skLineSegment(sketch, "E771", {"start": v(-7.38, -5.36) * mm, "end": v(-7, -5.7) * mm});
            skLineSegment(sketch, "E772", {"start": v(-7, -5.7) * mm, "end": v(-6.58, -5.99) * mm});
            skLineSegment(sketch, "E773", {"start": v(-6.58, -5.99) * mm, "end": v(-6.14, -6.29) * mm});
            skLineSegment(sketch, "E774", {"start": v(-6.14, -6.29) * mm, "end": v(-5.69, -6.54) * mm});
            skLineSegment(sketch, "E775", {"start": v(-5.69, -6.54) * mm, "end": v(-5.15, -6.8) * mm});
            skLineSegment(sketch, "E776", {"start": v(-5.15, -6.8) * mm, "end": v(-4.78, -6.95) * mm});
            skLineSegment(sketch, "E777", {"start": v(-4.78, -6.95) * mm, "end": v(-4.65, -6.98) * mm});
            skLineSegment(sketch, "E778", {"start": v(-4.65, -6.98) * mm, "end": v(-4.58, -6.95) * mm});
            skLineSegment(sketch, "E779", {"start": v(-4.58, -6.95) * mm, "end": v(-4.58, -6.6) * mm});
            skLineSegment(sketch, "E780", {"start": v(-4.58, -6.6) * mm, "end": v(-4.58, -5.78) * mm});
            skLineSegment(sketch, "E781", {"start": v(-4.58, -5.78) * mm, "end": v(-4.58, -5.23) * mm});
            skLineSegment(sketch, "E782", {"start": v(-4.58, -5.23) * mm, "end": v(-4.54, -4.36) * mm});
            skLineSegment(sketch, "E783", {"start": v(-4.54, -4.36) * mm, "end": v(-4.54, -3.78) * mm});
            skLineSegment(sketch, "E784", {"start": v(-4.54, -3.78) * mm, "end": v(-4.54, -3.26) * mm});
            skLineSegment(sketch, "E785", {"start": v(-4.54, -3.26) * mm, "end": v(-4.54, -3.16) * mm});
            skLineSegment(sketch, "E786", {"start": v(-4.54, -3.16) * mm, "end": v(-4.65, -3.1) * mm});
            skLineSegment(sketch, "E787", {"start": v(-4.65, -3.1) * mm, "end": v(-4.94, -3.02) * mm});
            skLineSegment(sketch, "E788", {"start": v(-4.94, -3.02) * mm, "end": v(-5.55, -2.82) * mm});
            skLineSegment(sketch, "E789", {"start": v(-5.55, -2.82) * mm, "end": v(-6.14, -2.61) * mm});
            skLineSegment(sketch, "E790", {"start": v(-6.14, -2.61) * mm, "end": v(-6.66, -2.4) * mm});
            skLineSegment(sketch, "E791", {"start": v(-6.66, -2.4) * mm, "end": v(-7.08, -2.2) * mm});
            skLineSegment(sketch, "E792", {"start": v(-7.08, -2.2) * mm, "end": v(-7.36, -2.06) * mm});
            skLineSegment(sketch, "E793", {"start": v(-7.36, -2.06) * mm, "end": v(-7.52, -1.96) * mm});
            skLineSegment(sketch, "E794", {"start": v(-3.72, -3.3) * mm, "end": v(-2.9, -3.45) * mm});
            skLineSegment(sketch, "E795", {"start": v(-2.9, -3.45) * mm, "end": v(-2.28, -3.55) * mm});
            skLineSegment(sketch, "E796", {"start": v(-2.28, -3.55) * mm, "end": v(-1.68, -3.62) * mm});
            skLineSegment(sketch, "E797", {"start": v(-1.68, -3.62) * mm, "end": v(-1.5, -3.64) * mm});
            skLineSegment(sketch, "E798", {"start": v(-1.5, -3.64) * mm, "end": v(-1.28, -3.64) * mm});
            skLineSegment(sketch, "E799", {"start": v(-1.28, -3.64) * mm, "end": v(-1.07, -3.66) * mm});
            skLineSegment(sketch, "E800", {"start": v(-1.07, -3.66) * mm, "end": v(-0.83, -3.67) * mm});
            skLineSegment(sketch, "E801", {"start": v(-0.83, -3.67) * mm, "end": v(-0.83, -4.6) * mm});
            skLineSegment(sketch, "E802", {"start": v(-0.83, -4.6) * mm, "end": v(-0.85, -5.33) * mm});
            skLineSegment(sketch, "E803", {"start": v(-0.85, -5.33) * mm, "end": v(-0.85, -5.86) * mm});
            skLineSegment(sketch, "E804", {"start": v(-0.85, -5.86) * mm, "end": v(-0.87, -6.44) * mm});
            skLineSegment(sketch, "E805", {"start": v(-0.87, -6.44) * mm, "end": v(-0.9, -7.17) * mm});
            skLineSegment(sketch, "E806", {"start": v(-0.9, -7.17) * mm, "end": v(-0.9, -7.7) * mm});
            skLineSegment(sketch, "E807", {"start": v(-0.9, -7.7) * mm, "end": v(-0.93, -7.8) * mm});
            skLineSegment(sketch, "E808", {"start": v(-0.93, -7.8) * mm, "end": v(-1.15, -7.8) * mm});
            skLineSegment(sketch, "E809", {"start": v(-1.15, -7.8) * mm, "end": v(-1.8, -7.69) * mm});
            skLineSegment(sketch, "E810", {"start": v(-1.8, -7.69) * mm, "end": v(-2.57, -7.57) * mm});
            skLineSegment(sketch, "E811", {"start": v(-2.57, -7.57) * mm, "end": v(-3.16, -7.43) * mm});
            skLineSegment(sketch, "E812", {"start": v(-3.16, -7.43) * mm, "end": v(-3.56, -7.33) * mm});
            skLineSegment(sketch, "E813", {"start": v(-3.56, -7.33) * mm, "end": v(-3.9, -7.24) * mm});
            skLineSegment(sketch, "E814", {"start": v(-3.9, -7.24) * mm, "end": v(-4.03, -7.19) * mm});
            skLineSegment(sketch, "E815", {"start": v(-4.03, -7.19) * mm, "end": v(-4.08, -7.19) * mm});
            skLineSegment(sketch, "E816", {"start": v(-4.08, -7.19) * mm, "end": v(-4.08, -7.04) * mm});
            skLineSegment(sketch, "E817", {"start": v(-4.08, -7.04) * mm, "end": v(-4.08, -6.51) * mm});
            skLineSegment(sketch, "E818", {"start": v(-4.08, -6.51) * mm, "end": v(-4.08, -5.92) * mm});
            skLineSegment(sketch, "E819", {"start": v(-4.08, -5.92) * mm, "end": v(-4.08, -5.54) * mm});
            skLineSegment(sketch, "E820", {"start": v(-4.08, -5.54) * mm, "end": v(-4.08, -4.81) * mm});
            skLineSegment(sketch, "E821", {"start": v(-4.08, -4.81) * mm, "end": v(-4.06, -4.21) * mm});
            skLineSegment(sketch, "E822", {"start": v(-4.06, -4.21) * mm, "end": v(-4.06, -3.77) * mm});
            skLineSegment(sketch, "E823", {"start": v(-4.06, -3.77) * mm, "end": v(-4.06, -3.4) * mm});
            skLineSegment(sketch, "E824", {"start": v(-4.06, -3.4) * mm, "end": v(-4.06, -3.33) * mm});
            skLineSegment(sketch, "E825", {"start": v(-4.06, -3.33) * mm, "end": v(-4.03, -3.27) * mm});
            skLineSegment(sketch, "E826", {"start": v(-4.03, -3.27) * mm, "end": v(-3.98, -3.24) * mm});
            skLineSegment(sketch, "E827", {"start": v(-3.98, -3.24) * mm, "end": v(-3.86, -3.26) * mm});
            skLineSegment(sketch, "E828", {"start": v(-3.86, -3.26) * mm, "end": v(-3.72, -3.3) * mm});
            skLineSegment(sketch, "E829", {"start": v(0.34, -3.7) * mm, "end": v(1.21, -3.67) * mm});
            skLineSegment(sketch, "E830", {"start": v(1.21, -3.67) * mm, "end": v(1.87, -3.62) * mm});
            skLineSegment(sketch, "E831", {"start": v(1.87, -3.62) * mm, "end": v(2.73, -3.55) * mm});
            skLineSegment(sketch, "E832", {"start": v(2.73, -3.55) * mm, "end": v(2.9, -3.51) * mm});
            skLineSegment(sketch, "E833", {"start": v(2.9, -3.51) * mm, "end": v(3.02, -3.52) * mm});
            skLineSegment(sketch, "E834", {"start": v(3.02, -3.52) * mm, "end": v(3.07, -3.58) * mm});
            skLineSegment(sketch, "E835", {"start": v(3.07, -3.58) * mm, "end": v(3.07, -4) * mm});
            skLineSegment(sketch, "E836", {"start": v(3.07, -4) * mm, "end": v(3.11, -4.85) * mm});
            skLineSegment(sketch, "E837", {"start": v(3.11, -4.85) * mm, "end": v(3.15, -5.77) * mm});
            skLineSegment(sketch, "E838", {"start": v(3.15, -5.77) * mm, "end": v(3.15, -6.5) * mm});
            skLineSegment(sketch, "E839", {"start": v(3.15, -6.5) * mm, "end": v(3.2, -7.15) * mm});
            skLineSegment(sketch, "E840", {"start": v(3.2, -7.15) * mm, "end": v(3.2, -7.32) * mm});
            skLineSegment(sketch, "E841", {"start": v(3.2, -7.32) * mm, "end": v(3.14, -7.4) * mm});
            skLineSegment(sketch, "E842", {"start": v(3.14, -7.4) * mm, "end": v(2.7, -7.5) * mm});
            skLineSegment(sketch, "E843", {"start": v(2.7, -7.5) * mm, "end": v(2.03, -7.65) * mm});
            skLineSegment(sketch, "E844", {"start": v(2.03, -7.65) * mm, "end": v(1.12, -7.77) * mm});
            skLineSegment(sketch, "E845", {"start": v(1.12, -7.77) * mm, "end": v(0.38, -7.82) * mm});
            skLineSegment(sketch, "E846", {"start": v(0.38, -7.82) * mm, "end": v(-0.1, -7.82) * mm});
            skLineSegment(sketch, "E847", {"start": v(-0.1, -7.82) * mm, "end": v(-0.28, -7.81) * mm});
            skLineSegment(sketch, "E848", {"start": v(-0.28, -7.81) * mm, "end": v(-0.43, -7.8) * mm});
            skLineSegment(sketch, "E849", {"start": v(-0.43, -7.8) * mm, "end": v(-0.43, -7.34) * mm});
            skLineSegment(sketch, "E850", {"start": v(-0.43, -7.34) * mm, "end": v(-0.4, -6.44) * mm});
            skLineSegment(sketch, "E851", {"start": v(-0.4, -6.44) * mm, "end": v(-0.37, -5.46) * mm});
            skLineSegment(sketch, "E852", {"start": v(-0.37, -5.46) * mm, "end": v(-0.35, -4.8) * mm});
            skLineSegment(sketch, "E853", {"start": v(-0.35, -4.8) * mm, "end": v(-0.33, -4.15) * mm});
            skLineSegment(sketch, "E854", {"start": v(-0.33, -4.15) * mm, "end": v(-0.33, -3.87) * mm});
            skLineSegment(sketch, "E855", {"start": v(-0.33, -3.87) * mm, "end": v(-0.32, -3.78) * mm});
            skLineSegment(sketch, "E856", {"start": v(-0.32, -3.78) * mm, "end": v(-0.26, -3.71) * mm});
            skLineSegment(sketch, "E857", {"start": v(-0.26, -3.71) * mm, "end": v(-0.2, -3.72) * mm});
            skLineSegment(sketch, "E858", {"start": v(-0.2, -3.72) * mm, "end": v(0.34, -3.7) * mm});
            skLineSegment(sketch, "E859", {"start": v(3.57, -3.42) * mm, "end": v(4.3, -3.25) * mm});
            skLineSegment(sketch, "E860", {"start": v(4.3, -3.25) * mm, "end": v(4.89, -3.14) * mm});
            skLineSegment(sketch, "E861", {"start": v(4.89, -3.14) * mm, "end": v(5.67, -2.88) * mm});
            skLineSegment(sketch, "E862", {"start": v(5.67, -2.88) * mm, "end": v(6.19, -2.72) * mm});
            skLineSegment(sketch, "E863", {"start": v(6.19, -2.72) * mm, "end": v(6.46, -2.62) * mm});
            skLineSegment(sketch, "E864", {"start": v(6.46, -2.62) * mm, "end": v(6.48, -3.03) * mm});
            skLineSegment(sketch, "E865", {"start": v(6.48, -3.03) * mm, "end": v(6.54, -4.26) * mm});
            skLineSegment(sketch, "E866", {"start": v(6.54, -4.26) * mm, "end": v(6.54, -5.22) * mm});
            skLineSegment(sketch, "E867", {"start": v(6.54, -5.22) * mm, "end": v(6.55, -5.5) * mm});
            skLineSegment(sketch, "E868", {"start": v(6.55, -5.5) * mm, "end": v(6.43, -5.67) * mm});
            skLineSegment(sketch, "E869", {"start": v(6.43, -5.67) * mm, "end": v(5.91, -6.07) * mm});
            skLineSegment(sketch, "E870", {"start": v(5.91, -6.07) * mm, "end": v(5.26, -6.48) * mm});
            skLineSegment(sketch, "E871", {"start": v(5.26, -6.48) * mm, "end": v(4.61, -6.83) * mm});
            skLineSegment(sketch, "E872", {"start": v(4.61, -6.83) * mm, "end": v(4.2, -7.02) * mm});
            skLineSegment(sketch, "E873", {"start": v(4.2, -7.02) * mm, "end": v(3.84, -7.17) * mm});
            skLineSegment(sketch, "E874", {"start": v(3.84, -7.17) * mm, "end": v(3.69, -7.17) * mm});
            skLineSegment(sketch, "E875", {"start": v(3.69, -7.17) * mm, "end": v(3.66, -6.65) * mm});
            skLineSegment(sketch, "E876", {"start": v(3.66, -6.65) * mm, "end": v(3.62, -5.78) * mm});
            skLineSegment(sketch, "E877", {"start": v(3.62, -5.78) * mm, "end": v(3.6, -5.04) * mm});
            skLineSegment(sketch, "E878", {"start": v(3.6, -5.04) * mm, "end": v(3.6, -4.6) * mm});
            skLineSegment(sketch, "E879", {"start": v(3.6, -4.6) * mm, "end": v(3.59, -4.18) * mm});
            skLineSegment(sketch, "E880", {"start": v(3.59, -4.18) * mm, "end": v(3.57, -3.83) * mm});
            skLineSegment(sketch, "E881", {"start": v(3.57, -3.83) * mm, "end": v(3.56, -3.51) * mm});
            skLineSegment(sketch, "E882", {"start": v(3.56, -3.51) * mm, "end": v(3.56, -3.45) * mm});
            skLineSegment(sketch, "E883", {"start": v(3.56, -3.45) * mm, "end": v(3.57, -3.42) * mm});
            skLineSegment(sketch, "E884", {"start": v(7.08, -2.35) * mm, "end": v(7.8, -2) * mm});
            skLineSegment(sketch, "E885", {"start": v(7.8, -2) * mm, "end": v(8.41, -1.64) * mm});
            skLineSegment(sketch, "E886", {"start": v(8.41, -1.64) * mm, "end": v(8.85, -1.3) * mm});
            skLineSegment(sketch, "E887", {"start": v(8.85, -1.3) * mm, "end": v(9.04, -1.16) * mm});
            skLineSegment(sketch, "E888", {"start": v(9.04, -1.16) * mm, "end": v(9.08, -1.21) * mm});
            skLineSegment(sketch, "E889", {"start": v(9.08, -1.21) * mm, "end": v(9.08, -1.33) * mm});
            skLineSegment(sketch, "E890", {"start": v(9.08, -1.33) * mm, "end": v(8.97, -1.74) * mm});
            skLineSegment(sketch, "E891", {"start": v(8.97, -1.74) * mm, "end": v(8.7, -2.56) * mm});
            skLineSegment(sketch, "E892", {"start": v(8.7, -2.56) * mm, "end": v(8.44, -3.15) * mm});
            skLineSegment(sketch, "E893", {"start": v(8.44, -3.15) * mm, "end": v(8.14, -3.67) * mm});
            skLineSegment(sketch, "E894", {"start": v(8.14, -3.67) * mm, "end": v(7.86, -4.1) * mm});
            skLineSegment(sketch, "E895", {"start": v(7.86, -4.1) * mm, "end": v(7.52, -4.56) * mm});
            skLineSegment(sketch, "E896", {"start": v(7.52, -4.56) * mm, "end": v(7.29, -4.85) * mm});
            skLineSegment(sketch, "E897", {"start": v(7.29, -4.85) * mm, "end": v(7.14, -4.96) * mm});
            skLineSegment(sketch, "E898", {"start": v(7.14, -4.96) * mm, "end": v(7.03, -5.04) * mm});
            skLineSegment(sketch, "E899", {"start": v(7.03, -5.04) * mm, "end": v(7.01, -4.66) * mm});
            skLineSegment(sketch, "E900", {"start": v(7.01, -4.66) * mm, "end": v(7, -4.03) * mm});
            skLineSegment(sketch, "E901", {"start": v(7, -4.03) * mm, "end": v(6.98, -3.62) * mm});
            skLineSegment(sketch, "E902", {"start": v(6.98, -3.62) * mm, "end": v(6.99, -3.1) * mm});
            skPoint(sketch, "E902.endSnap0", {"position": v(6.99, -3.82) * mm});
            skLineSegment(sketch, "E903", {"start": v(6.99, -3.1) * mm, "end": v(6.97, -2.65) * mm});
            skLineSegment(sketch, "E904", {"start": v(6.97, -2.65) * mm, "end": v(6.98, -2.47) * mm});
            skLineSegment(sketch, "E905", {"start": v(6.98, -2.47) * mm, "end": v(7, -2.4) * mm});
            skLineSegment(sketch, "E906", {"start": v(7, -2.4) * mm, "end": v(7.08, -2.35) * mm});
            skSolve(sketch);
        }
        {
            var Q0;
            Q0 = qSketchRegion(id + "F6", true);
            extrude(context, id + "F7", {"entities" : qUnion([Q0]), "operationType" : NewBodyOperationType.REMOVE, "depth" : 25 * mm});
        }
    });
